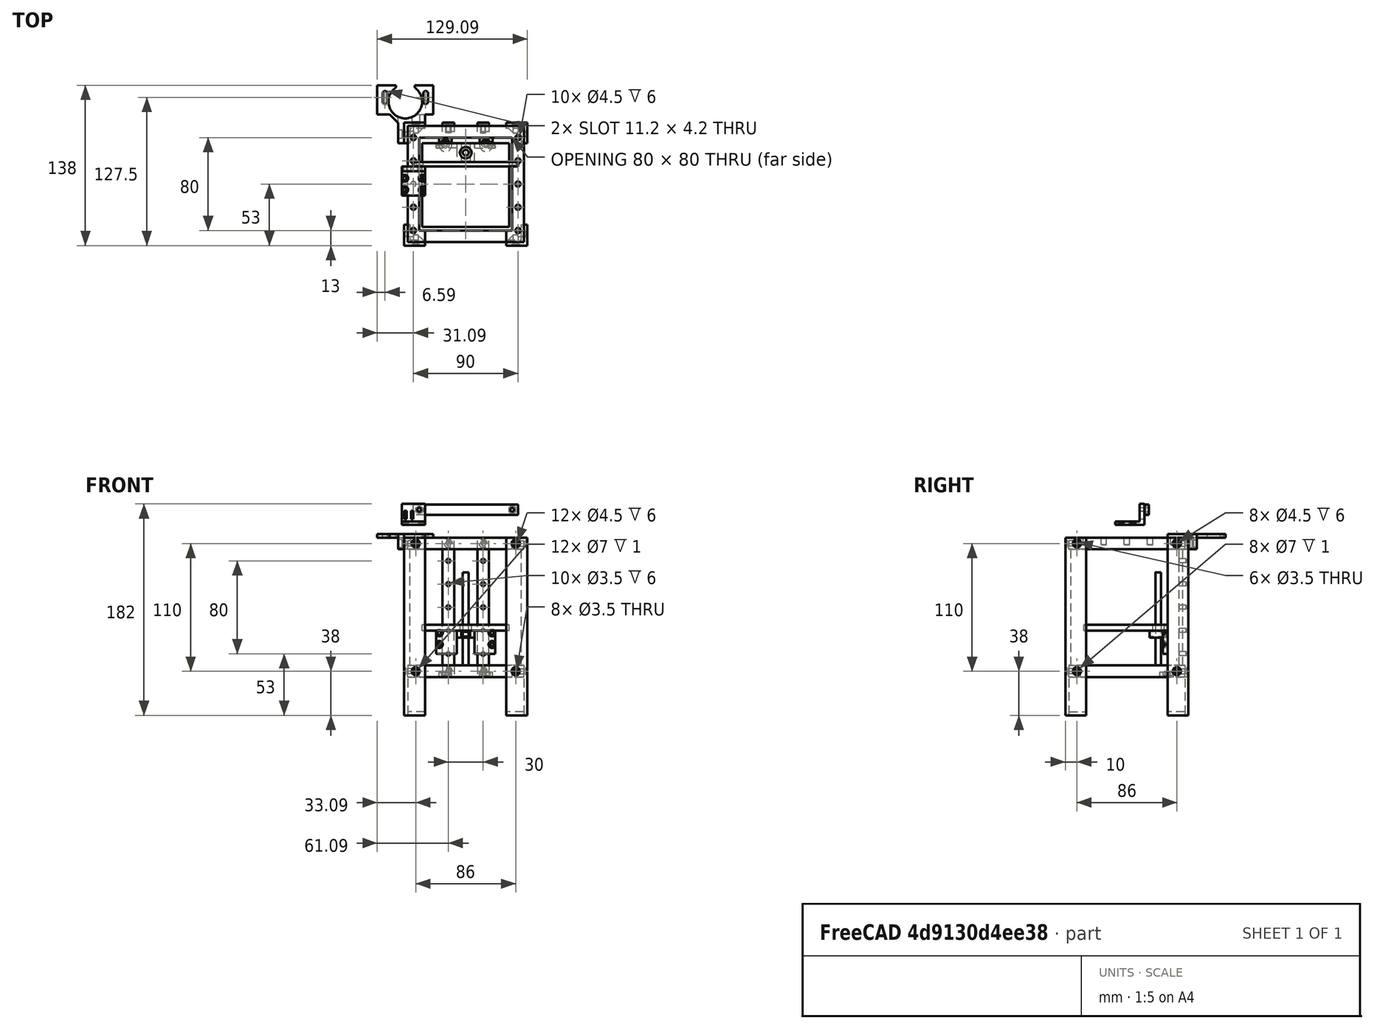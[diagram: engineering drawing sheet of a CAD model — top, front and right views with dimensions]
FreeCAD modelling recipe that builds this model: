
FCSTD DOCUMENT  (FreeCAD 0.19R24267 +99 (Git))
Label: cad
License: All rights reserved
LicenseURL: http://en.wikipedia.org/wiki/All_rights_reserved
objects: Sketcher::SketchObject×95, PartDesign::Pocket×61, PartDesign::Pad×34, Mesh::Feature×14, PartDesign::Body×13, PartDesign::Mirrored×6, PartDesign::PolarPattern×4
note: 308 computed .brp shape members not serialized (recipe doc carries the construction recipe); baked Part::Feature solids carry a one-line shape summary decoded from their .brp

FEATURE [Sketcher::SketchObject] Sketch
  FullyConstrained = true
  MapMode = 5
  Support = -> [XY_Plane]
  sketch-geometry (8):
    g0: LineSegment StartX=-50 StartY=50 StartZ=0 EndX=50 EndY=50 EndZ=0
    g1: LineSegment StartX=50 StartY=50 StartZ=0 EndX=50 EndY=-50 EndZ=0
    g2: LineSegment StartX=50 StartY=-50 StartZ=0 EndX=-50 EndY=-50 EndZ=0
    g3: LineSegment StartX=-50 StartY=-50 StartZ=0 EndX=-50 EndY=50 EndZ=0
    g4: LineSegment StartX=-40 StartY=40 StartZ=0 EndX=40 EndY=40 EndZ=0
    g5: LineSegment StartX=40 StartY=40 StartZ=0 EndX=40 EndY=-40 EndZ=0
    g6: LineSegment StartX=40 StartY=-40 StartZ=0 EndX=-40 EndY=-40 EndZ=0
    g7: LineSegment StartX=-40 StartY=-40 StartZ=0 EndX=-40 EndY=40 EndZ=0
  constraints (20):
    c: Coincident(g0,g1)
    c: Coincident(g1,g2)
    c: Coincident(g2,g3)
    c: Coincident(g3,g0)
    c: Horizontal(g2)
    c: Vertical(g1)
    c: Coincident(g4,g5)
    c: Coincident(g5,g6)
    c: Coincident(g6,g7)
    c: Coincident(g7,g4)
    c: Horizontal(g6)
    c: Vertical(g5)
    c: Symmetric(g4,g4,g-2)
    c: Symmetric(g4,g6,g-1)
    c: Equal(g7,g4)
    c: Equal(g0,g3)
    c: Symmetric(g0,g2,g-1)
    c: Symmetric(g0,g0,g-2)
    c: DistanceY(g4,g0) = 10
    c: DistanceY(g3,g3) = 100
FEATURE [PartDesign::Pad] Pad
  Direction = (1,1,1)
  Length = 10
  Length2 = 100
  Profile = -> Sketch
  Type = 0
FEATURE [Sketcher::SketchObject] Sketch002
  ExternalGeometry = -> [Pad]
  FullyConstrained = true
  MapMode = 5
  Placement = pos=(0,0,10) rot=(0,0,1;0rad)
  Support = -> [Pad]
  sketch-geometry (9):
    g0: Circle CenterX=-45 CenterY=40 CenterZ=0 NormalX=0 NormalY=0 NormalZ=1 AngleXU=0 Radius=2.25
    g1: LineSegment StartX=-45 StartY=40 StartZ=0 EndX=-50 EndY=40 EndZ=0
    g2: LineSegment StartX=-40 StartY=40 StartZ=0 EndX=-40 EndY=50 EndZ=0
    g3: LineSegment StartX=-45 StartY=40 StartZ=0 EndX=-40 EndY=40 EndZ=0
    g4: Circle CenterX=-45 CenterY=20 CenterZ=0 NormalX=0 NormalY=0 NormalZ=1 AngleXU=0 Radius=2.25
    g5: Circle CenterX=-45 CenterY=1.8e-15 CenterZ=0 NormalX=0 NormalY=0 NormalZ=1 AngleXU=0 Radius=2.25
    g6: Circle CenterX=-45 CenterY=-20 CenterZ=0 NormalX=0 NormalY=0 NormalZ=1 AngleXU=0 Radius=2.25
    g7: Circle CenterX=-45 CenterY=-40 CenterZ=0 NormalX=0 NormalY=0 NormalZ=1 AngleXU=0 Radius=2.25
    g8: LineSegment StartX=-45 StartY=40 StartZ=0 EndX=-45 EndY=-50 EndZ=0
  constraints (27):
    c: Radius(g0) = 2.25
    c: Coincident(g1,g0)
    c: PointOnObject(g1,g-3)
    c: Horizontal(g1)
    c: Coincident(g2,g-4)
    c: Vertical(g2)
    c: Coincident(g3,g0)
    c: Horizontal(g3)
    c: PointOnObject(g3,g2)
    c: Equal(g1,g3)
    c: DistanceY(g0,g-3) = 10
    c: PointOnObject(g2,g-5)
    c: Equal(g0,g4)
    c: Equal(g4,g5)
    c: Equal(g5,g6)
    c: Equal(g6,g7)
    c: Coincident(g8,g0)
    c: PointOnObject(g8,g-6)
    c: Vertical(g8)
    c: PointOnObject(g7,g8)
    c: PointOnObject(g6,g8)
    c: PointOnObject(g5,g8)
    c: PointOnObject(g4,g8)
    c: DistanceY(g4,g0) = 20
    c: DistanceY(g5,g4) = 20
    c: DistanceY(g6,g5) = 20
    c: DistanceY(g7,g6) = 20
FEATURE [PartDesign::Pocket] Pocket
  BaseFeature = -> Pad
  Length = 6
  Length2 = 100
  Profile = -> Sketch002
  Type = 0
FEATURE [PartDesign::Mirrored] Mirrored
  BaseFeature = -> Pocket
  MirrorPlane = -> Sketch002 [V_Axis]
  Originals = -> [Pocket]
FEATURE [Sketcher::SketchObject] Sketch003
  FullyConstrained = true
  MapMode = 5
  Support = -> [XY_Plane002]
  sketch-geometry (4):
    g0: LineSegment StartX=-20 StartY=53 StartZ=0 EndX=-10 EndY=53 EndZ=0
    g1: LineSegment StartX=-10 StartY=53 StartZ=0 EndX=-10 EndY=45 EndZ=0
    g2: LineSegment StartX=-10 StartY=45 StartZ=0 EndX=-20 EndY=45 EndZ=0
    g3: LineSegment StartX=-20 StartY=45 StartZ=0 EndX=-20 EndY=53 EndZ=0
  constraints (12):
    c: Coincident(g0,g1)
    c: Coincident(g1,g2)
    c: Coincident(g2,g3)
    c: Coincident(g3,g0)
    c: Horizontal(g0)
    c: Horizontal(g2)
    c: Vertical(g1)
    c: Vertical(g3)
    c: DistanceY(g3,g3) = 8
    c: DistanceY(g-1,g1) = 45
    c: DistanceX(g0,g0) = 10
    c: DistanceX(g0,g-1) = 10
FEATURE [PartDesign::Pad] Pad002
  Direction = (1,1,1)
  Length = 100
  Length2 = 100
  Profile = -> Sketch003
  Type = 0
FEATURE [Sketcher::SketchObject] Sketch004
  ExternalGeometry = -> [Pad002]
  FullyConstrained = true
  MapMode = 5
  Placement = pos=(0,0,100) rot=(0,0,1;0rad)
  Support = -> [Pad002]
  sketch-geometry (4):
    g0: LineSegment StartX=-10 StartY=53 StartZ=0 EndX=-20 EndY=53 EndZ=0
    g1: LineSegment StartX=-20 StartY=53 StartZ=0 EndX=-20 EndY=50 EndZ=0
    g2: LineSegment StartX=-20 StartY=50 StartZ=0 EndX=-10 EndY=50 EndZ=0
    g3: LineSegment StartX=-10 StartY=50 StartZ=0 EndX=-10 EndY=53 EndZ=0
  constraints (11):
    c: Coincident(g0,g1)
    c: Coincident(g1,g2)
    c: Coincident(g2,g3)
    c: Coincident(g3,g0)
    c: Horizontal(g0)
    c: Horizontal(g2)
    c: Vertical(g1)
    c: Vertical(g3)
    c: Coincident(g0,g-3)
    c: PointOnObject(g1,g-4)
    c: DistanceY(g3,g3) = 3
FEATURE [PartDesign::Pad] Pad003
  BaseFeature = -> Pad002
  Direction = (1,1,1)
  Length = 10
  Length2 = 100
  Profile = -> Sketch004
  Type = 0
FEATURE [Sketcher::SketchObject] Sketch005
  ExternalGeometry = -> [Pad003]
  FullyConstrained = true
  MapMode = 5
  Placement = pos=(0,53,0) rot=(0,0.707107,0.707107;3.14159rad)
  Support = -> [Pad003]
  sketch-geometry (4):
    g0: Circle CenterX=15 CenterY=105 CenterZ=0 NormalX=0 NormalY=0 NormalZ=1 AngleXU=0 Radius=1.7
    g1: LineSegment StartX=15 StartY=105 StartZ=0 EndX=10 EndY=110 EndZ=0
    g2: LineSegment StartX=15 StartY=105 StartZ=0 EndX=10 EndY=100 EndZ=0
    g3: LineSegment StartX=15 StartY=105 StartZ=0 EndX=20 EndY=110 EndZ=0
  constraints (9):
    c: Radius(g0) = 1.7
    c: Coincident(g1,g-3)
    c: Coincident(g2,g-3)
    c: Coincident(g3,g-4)
    c: Equal(g1,g3)
    c: Equal(g3,g2)
    c: Coincident(g0,g1)
    c: Coincident(g0,g3)
    c: Coincident(g0,g2)
FEATURE [PartDesign::Pocket] Pocket001
  BaseFeature = -> Pad003
  Length = 5
  Length2 = 100
  Profile = -> Sketch005
  Type = 0
FEATURE [Sketcher::SketchObject] Sketch006
  ExternalGeometry = -> [Pocket001]
  FullyConstrained = true
  MapMode = 5
  Placement = pos=(0,53,0) rot=(0,0.707107,0.707107;3.14159rad)
  Support = -> [Pocket001]
  sketch-geometry (1):
    g0: Circle CenterX=15 CenterY=105 CenterZ=0 NormalX=0 NormalY=0 NormalZ=1 AngleXU=0 Radius=3.5
  constraints (2):
    c: Coincident(g0,g-3)
    c: Radius(g0) = 3.5
FEATURE [PartDesign::Pocket] Pocket002
  BaseFeature = -> Pocket001
  Length = 1
  Length2 = 100
  Profile = -> Sketch006
  Type = 0
FEATURE [Sketcher::SketchObject] Sketch007
  ExternalGeometry = -> [Pocket002]
  FullyConstrained = true
  MapMode = 5
  Placement = pos=(0,0,0) rot=(1,0,0;3.14159rad)
  Support = -> [Pocket002]
  sketch-geometry (4):
    g0: LineSegment StartX=-10 StartY=-53 StartZ=0 EndX=-20 EndY=-53 EndZ=0
    g1: LineSegment StartX=-20 StartY=-53 StartZ=0 EndX=-20 EndY=-50 EndZ=0
    g2: LineSegment StartX=-20 StartY=-50 StartZ=0 EndX=-10 EndY=-50 EndZ=0
    g3: LineSegment StartX=-10 StartY=-50 StartZ=0 EndX=-10 EndY=-53 EndZ=0
  constraints (11):
    c: Coincident(g0,g1)
    c: Coincident(g1,g2)
    c: Coincident(g2,g3)
    c: Coincident(g3,g0)
    c: Horizontal(g0)
    c: Horizontal(g2)
    c: Vertical(g1)
    c: Vertical(g3)
    c: Coincident(g0,g-4)
    c: PointOnObject(g1,g-3)
    c: DistanceY(g3,g3) = 3
FEATURE [PartDesign::Pad] Pad004
  BaseFeature = -> Pocket002
  Direction = (1,1,1)
  Length = 10
  Length2 = 100
  Profile = -> Sketch007
  Type = 0
FEATURE [Sketcher::SketchObject] Sketch008
  ExternalGeometry = -> [Pad004]
  FullyConstrained = true
  MapMode = 5
  Placement = pos=(0,53,0) rot=(0,0.707107,0.707107;3.14159rad)
  Support = -> [Pad004]
  sketch-geometry (4):
    g0: Circle CenterX=15 CenterY=-5 CenterZ=0 NormalX=0 NormalY=0 NormalZ=1 AngleXU=0 Radius=1.75
    g1: LineSegment StartX=15 StartY=-5 StartZ=0 EndX=10 EndY=0 EndZ=0
    g2: LineSegment StartX=15 StartY=-5 StartZ=0 EndX=10 EndY=-10 EndZ=0
    g3: LineSegment StartX=15 StartY=-5 StartZ=0 EndX=20 EndY=-10 EndZ=0
  constraints (9):
    c: Coincident(g1,g0)
    c: Coincident(g1,g-3)
    c: Coincident(g2,g0)
    c: Coincident(g2,g-4)
    c: Coincident(g3,g0)
    c: Coincident(g3,g-4)
    c: Equal(g3,g2)
    c: Equal(g2,g1)
    c: Radius(g0) = 1.75
FEATURE [PartDesign::Pocket] Pocket003
  BaseFeature = -> Pad004
  Length = 5
  Length2 = 100
  Profile = -> Sketch008
  Type = 0
FEATURE [Sketcher::SketchObject] Sketch009
  ExternalGeometry = -> [Pocket003]
  FullyConstrained = true
  MapMode = 5
  Placement = pos=(0,53,0) rot=(0,0.707107,0.707107;3.14159rad)
  Support = -> [Pocket003]
  sketch-geometry (1):
    g0: Circle CenterX=15 CenterY=-5 CenterZ=0 NormalX=0 NormalY=0 NormalZ=1 AngleXU=0 Radius=3.5
  constraints (2):
    c: Coincident(g0,g-3)
    c: Radius(g0) = 3.5
FEATURE [PartDesign::Pocket] Pocket004
  BaseFeature = -> Pocket003
  Length = 1
  Length2 = 100
  Profile = -> Sketch009
  Type = 0
FEATURE [Sketcher::SketchObject] Sketch010
  ExternalGeometry = -> [Pocket004]
  FullyConstrained = true
  MapMode = 5
  Placement = pos=(0,45,0) rot=(1,0,0;1.5708rad)
  Support = -> [Pocket004]
  sketch-geometry (6):
    g0: Circle CenterX=-15 CenterY=90 CenterZ=0 NormalX=0 NormalY=0 NormalZ=1 AngleXU=0 Radius=1.75
    g1: Circle CenterX=-15 CenterY=70 CenterZ=0 NormalX=0 NormalY=0 NormalZ=1 AngleXU=0 Radius=1.75
    g2: Circle CenterX=-15 CenterY=50 CenterZ=0 NormalX=0 NormalY=0 NormalZ=1 AngleXU=0 Radius=1.75
    g3: Circle CenterX=-15 CenterY=30 CenterZ=0 NormalX=0 NormalY=0 NormalZ=1 AngleXU=0 Radius=1.75
    g4: Circle CenterX=-15 CenterY=10 CenterZ=0 NormalX=0 NormalY=0 NormalZ=1 AngleXU=0 Radius=1.75
    g5: LineSegment StartX=-15 StartY=100 StartZ=0 EndX=-15 EndY=0 EndZ=0
  constraints (19):
    c: Equal(g0,g1)
    c: Equal(g1,g2)
    c: Equal(g2,g3)
    c: Equal(g3,g4)
    c: Radius(g0) = 1.75
    c: PointOnObject(g5,g-5)
    c: PointOnObject(g5,g-1)
    c: Vertical(g5)
    c: DistanceX(g-5,g5) = 5
    c: PointOnObject(g0,g5)
    c: PointOnObject(g1,g5)
    c: PointOnObject(g2,g5)
    c: PointOnObject(g3,g5)
    c: PointOnObject(g4,g5)
    c: DistanceY(g1,g0) = 20
    c: DistanceY(g2,g1) = 20
    c: DistanceY(g3,g2) = 20
    c: DistanceY(g4,g3) = 20
    c: DistanceY(g0,g5) = 10
FEATURE [PartDesign::Pocket] Pocket005
  BaseFeature = -> Pocket004
  Length = 6
  Length2 = 100
  Profile = -> Sketch010
  Type = 0
FEATURE [PartDesign::Body] Body002  label="z_rail"
  Group = -> [Sketch003,Pad002,Sketch004,Pad003,Sketch005,Pocket001,Sketch006,Pocket002,Sketch007,Pad004,Sketch008,Pocket003,Sketch009,Pocket004,Sketch010,Pocket005]
  Origin = -> Origin002
  Tip = -> Pocket005
FEATURE [Sketcher::SketchObject] Sketch016
  FullyConstrained = true
  MapMode = 5
  Support = -> [XY_Plane003]
  sketch-geometry (4):
    g0: LineSegment StartX=-20 StartY=53 StartZ=0 EndX=-10 EndY=53 EndZ=0
    g1: LineSegment StartX=-10 StartY=53 StartZ=0 EndX=-10 EndY=45 EndZ=0
    g2: LineSegment StartX=-10 StartY=45 StartZ=0 EndX=-20 EndY=45 EndZ=0
    g3: LineSegment StartX=-20 StartY=45 StartZ=0 EndX=-20 EndY=53 EndZ=0
  constraints (12):
    c: Coincident(g0,g1)
    c: Coincident(g1,g2)
    c: Coincident(g2,g3)
    c: Coincident(g3,g0)
    c: Horizontal(g0)
    c: Horizontal(g2)
    c: Vertical(g1)
    c: Vertical(g3)
    c: DistanceY(g3,g3) = 8
    c: DistanceY(g-1,g1) = 45
    c: DistanceX(g0,g0) = 10
    c: DistanceX(g0,g-1) = 10
FEATURE [PartDesign::Pad] Pad005
  Direction = (1,1,1)
  Length = 100
  Length2 = 100
  Profile = -> Sketch016
  Type = 0
FEATURE [Sketcher::SketchObject] Sketch015
  ExternalGeometry = -> [Pad005]
  FullyConstrained = true
  MapMode = 5
  Placement = pos=(0,0,100) rot=(0,0,1;0rad)
  Support = -> [Pad005]
  sketch-geometry (4):
    g0: LineSegment StartX=-10 StartY=53 StartZ=0 EndX=-20 EndY=53 EndZ=0
    g1: LineSegment StartX=-20 StartY=53 StartZ=0 EndX=-20 EndY=50 EndZ=0
    g2: LineSegment StartX=-20 StartY=50 StartZ=0 EndX=-10 EndY=50 EndZ=0
    g3: LineSegment StartX=-10 StartY=50 StartZ=0 EndX=-10 EndY=53 EndZ=0
  constraints (11):
    c: Coincident(g0,g1)
    c: Coincident(g1,g2)
    c: Coincident(g2,g3)
    c: Coincident(g3,g0)
    c: Horizontal(g0)
    c: Horizontal(g2)
    c: Vertical(g1)
    c: Vertical(g3)
    c: Coincident(g0,g-3)
    c: PointOnObject(g1,g-4)
    c: DistanceY(g3,g3) = 3
FEATURE [PartDesign::Pad] Pad006
  BaseFeature = -> Pad005
  Direction = (1,1,1)
  Length = 10
  Length2 = 100
  Profile = -> Sketch015
  Type = 0
FEATURE [Sketcher::SketchObject] Sketch017
  ExternalGeometry = -> [Pad006]
  FullyConstrained = true
  MapMode = 5
  Placement = pos=(0,53,0) rot=(0,0.707107,0.707107;3.14159rad)
  Support = -> [Pad006]
  sketch-geometry (4):
    g0: Circle CenterX=15 CenterY=105 CenterZ=0 NormalX=0 NormalY=0 NormalZ=1 AngleXU=0 Radius=1.7
    g1: LineSegment StartX=15 StartY=105 StartZ=0 EndX=10 EndY=110 EndZ=0
    g2: LineSegment StartX=15 StartY=105 StartZ=0 EndX=10 EndY=100 EndZ=0
    g3: LineSegment StartX=15 StartY=105 StartZ=0 EndX=20 EndY=110 EndZ=0
  constraints (9):
    c: Radius(g0) = 1.7
    c: Coincident(g1,g-3)
    c: Coincident(g2,g-3)
    c: Coincident(g3,g-4)
    c: Equal(g1,g3)
    c: Equal(g3,g2)
    c: Coincident(g0,g1)
    c: Coincident(g0,g3)
    c: Coincident(g0,g2)
FEATURE [PartDesign::Pocket] Pocket006
  BaseFeature = -> Pad006
  Length = 5
  Length2 = 100
  Profile = -> Sketch017
  Type = 0
FEATURE [Sketcher::SketchObject] Sketch013
  ExternalGeometry = -> [Pocket006]
  FullyConstrained = true
  MapMode = 5
  Placement = pos=(0,53,0) rot=(0,0.707107,0.707107;3.14159rad)
  Support = -> [Pocket006]
  sketch-geometry (1):
    g0: Circle CenterX=15 CenterY=105 CenterZ=0 NormalX=0 NormalY=0 NormalZ=1 AngleXU=0 Radius=3.5
  constraints (2):
    c: Coincident(g0,g-3)
    c: Radius(g0) = 3.5
FEATURE [PartDesign::Pocket] Pocket008
  BaseFeature = -> Pocket006
  Length = 1
  Length2 = 100
  Profile = -> Sketch013
  Type = 0
FEATURE [Sketcher::SketchObject] Sketch012
  ExternalGeometry = -> [Pocket008]
  FullyConstrained = true
  MapMode = 5
  Placement = pos=(0,0,0) rot=(1,0,0;3.14159rad)
  Support = -> [Pocket008]
  sketch-geometry (4):
    g0: LineSegment StartX=-10 StartY=-53 StartZ=0 EndX=-20 EndY=-53 EndZ=0
    g1: LineSegment StartX=-20 StartY=-53 StartZ=0 EndX=-20 EndY=-50 EndZ=0
    g2: LineSegment StartX=-20 StartY=-50 StartZ=0 EndX=-10 EndY=-50 EndZ=0
    g3: LineSegment StartX=-10 StartY=-50 StartZ=0 EndX=-10 EndY=-53 EndZ=0
  constraints (11):
    c: Coincident(g0,g1)
    c: Coincident(g1,g2)
    c: Coincident(g2,g3)
    c: Coincident(g3,g0)
    c: Horizontal(g0)
    c: Horizontal(g2)
    c: Vertical(g1)
    c: Vertical(g3)
    c: Coincident(g0,g-4)
    c: PointOnObject(g1,g-3)
    c: DistanceY(g3,g3) = 3
FEATURE [PartDesign::Pad] Pad007
  BaseFeature = -> Pocket008
  Direction = (1,1,1)
  Length = 10
  Length2 = 100
  Profile = -> Sketch012
  Type = 0
FEATURE [Sketcher::SketchObject] Sketch011
  ExternalGeometry = -> [Pad007]
  FullyConstrained = true
  MapMode = 5
  Placement = pos=(0,53,0) rot=(0,0.707107,0.707107;3.14159rad)
  Support = -> [Pad007]
  sketch-geometry (4):
    g0: Circle CenterX=15 CenterY=-5 CenterZ=0 NormalX=0 NormalY=0 NormalZ=1 AngleXU=0 Radius=1.75
    g1: LineSegment StartX=15 StartY=-5 StartZ=0 EndX=10 EndY=0 EndZ=0
    g2: LineSegment StartX=15 StartY=-5 StartZ=0 EndX=10 EndY=-10 EndZ=0
    g3: LineSegment StartX=15 StartY=-5 StartZ=0 EndX=20 EndY=-10 EndZ=0
  constraints (9):
    c: Coincident(g1,g0)
    c: Coincident(g1,g-3)
    c: Coincident(g2,g0)
    c: Coincident(g2,g-4)
    c: Coincident(g3,g0)
    c: Coincident(g3,g-4)
    c: Equal(g3,g2)
    c: Equal(g2,g1)
    c: Radius(g0) = 1.75
FEATURE [PartDesign::Pocket] Pocket007
  BaseFeature = -> Pad007
  Length = 5
  Length2 = 100
  Profile = -> Sketch011
  Type = 0
FEATURE [Sketcher::SketchObject] Sketch014
  ExternalGeometry = -> [Pocket007]
  FullyConstrained = true
  MapMode = 5
  Placement = pos=(0,53,0) rot=(0,0.707107,0.707107;3.14159rad)
  Support = -> [Pocket007]
  sketch-geometry (1):
    g0: Circle CenterX=15 CenterY=-5 CenterZ=0 NormalX=0 NormalY=0 NormalZ=1 AngleXU=0 Radius=3.5
  constraints (2):
    c: Coincident(g0,g-3)
    c: Radius(g0) = 3.5
FEATURE [PartDesign::Pocket] Pocket010
  BaseFeature = -> Pocket007
  Length = 1
  Length2 = 100
  Profile = -> Sketch014
  Type = 0
FEATURE [Sketcher::SketchObject] Sketch018
  ExternalGeometry = -> [Pocket010]
  FullyConstrained = true
  MapMode = 5
  Placement = pos=(0,45,0) rot=(1,0,0;1.5708rad)
  Support = -> [Pocket010]
  sketch-geometry (6):
    g0: Circle CenterX=-15 CenterY=90 CenterZ=0 NormalX=0 NormalY=0 NormalZ=1 AngleXU=0 Radius=1.75
    g1: Circle CenterX=-15 CenterY=70 CenterZ=0 NormalX=0 NormalY=0 NormalZ=1 AngleXU=0 Radius=1.75
    g2: Circle CenterX=-15 CenterY=50 CenterZ=0 NormalX=0 NormalY=0 NormalZ=1 AngleXU=0 Radius=1.75
    g3: Circle CenterX=-15 CenterY=30 CenterZ=0 NormalX=0 NormalY=0 NormalZ=1 AngleXU=0 Radius=1.75
    g4: Circle CenterX=-15 CenterY=10 CenterZ=0 NormalX=0 NormalY=0 NormalZ=1 AngleXU=0 Radius=1.75
    g5: LineSegment StartX=-15 StartY=100 StartZ=0 EndX=-15 EndY=0 EndZ=0
  constraints (19):
    c: Equal(g0,g1)
    c: Equal(g1,g2)
    c: Equal(g2,g3)
    c: Equal(g3,g4)
    c: Radius(g0) = 1.75
    c: PointOnObject(g5,g-5)
    c: PointOnObject(g5,g-1)
    c: Vertical(g5)
    c: DistanceX(g-5,g5) = 5
    c: PointOnObject(g0,g5)
    c: PointOnObject(g1,g5)
    c: PointOnObject(g2,g5)
    c: PointOnObject(g3,g5)
    c: PointOnObject(g4,g5)
    c: DistanceY(g1,g0) = 20
    c: DistanceY(g2,g1) = 20
    c: DistanceY(g3,g2) = 20
    c: DistanceY(g4,g3) = 20
    c: DistanceY(g0,g5) = 10
FEATURE [PartDesign::Pocket] Pocket009
  BaseFeature = -> Pocket010
  Length = 6
  Length2 = 100
  Profile = -> Sketch018
  Type = 0
FEATURE [PartDesign::Body] Body003  label="z_rail001"
  Group = -> [Sketch016,Pad005,Sketch015,Pad006,Sketch017,Pocket006,Sketch013,Pocket008,Sketch012,Pad007,Sketch011,Pocket007,Sketch014,Pocket010,Sketch018,Pocket009]
  Origin = -> Origin003
  Placement = pos=(30,0,0) rot=(0,0,1;0rad)
  Tip = -> Pocket009
FEATURE [Sketcher::SketchObject] Sketch019
  FullyConstrained = true
  MapMode = 5
  Support = -> [XY_Plane004]
  sketch-geometry (6):
    g0: LineSegment StartX=-53 StartY=-35 StartZ=0 EndX=-53 EndY=-53 EndZ=0
    g1: LineSegment StartX=-53 StartY=-53 StartZ=0 EndX=-35 EndY=-53 EndZ=0
    g2: LineSegment StartX=-48 StartY=-35 StartZ=0 EndX=-48 EndY=-48 EndZ=0
    g3: LineSegment StartX=-48 StartY=-48 StartZ=0 EndX=-35 EndY=-48 EndZ=0
    g4: LineSegment StartX=-48 StartY=-35 StartZ=0 EndX=-53 EndY=-35 EndZ=0
    g5: LineSegment StartX=-35 StartY=-48 StartZ=0 EndX=-35 EndY=-53 EndZ=0
  constraints (19):
    c: Vertical(g0)
    c: Coincident(g1,g0)
    c: Horizontal(g1)
    c: DistanceY(g0,g-1) = 53
    c: DistanceX(g0,g-1) = 53
    c: Vertical(g2)
    c: Coincident(g3,g2)
    c: Horizontal(g3)
    c: DistanceY(g0,g2) = 5
    c: DistanceX(g0,g2) = 5
    c: Coincident(g4,g2)
    c: Horizontal(g4)
    c: Vertical(g5)
    c: Coincident(g0,g4)
    c: Coincident(g1,g5)
    c: Equal(g0,g1)
    c: Equal(g2,g3)
    c: Equal(g4,g5)
    c: DistanceY(g0,g0) = 18
FEATURE [PartDesign::Pad] Pad008
  Direction = (1,1,1)
  Length = 100
  Length2 = 100
  Profile = -> Sketch019
  Type = 0
FEATURE [Sketcher::SketchObject] Sketch020
  ExternalGeometry = -> [Pad008]
  FullyConstrained = true
  MapMode = 5
  Placement = pos=(0,0,100) rot=(0,0,1;0rad)
  Support = -> [Pad008]
  sketch-geometry (6):
    g0: LineSegment StartX=-53 StartY=-35 StartZ=0 EndX=-53 EndY=-53 EndZ=0
    g1: LineSegment StartX=-53 StartY=-53 StartZ=0 EndX=-35 EndY=-53 EndZ=0
    g2: LineSegment StartX=-35 StartY=-53 StartZ=0 EndX=-35 EndY=-50 EndZ=0
    g3: LineSegment StartX=-35 StartY=-50 StartZ=0 EndX=-50 EndY=-50 EndZ=0
    g4: LineSegment StartX=-50 StartY=-50 StartZ=0 EndX=-50 EndY=-35 EndZ=0
    g5: LineSegment StartX=-50 StartY=-35 StartZ=0 EndX=-53 EndY=-35 EndZ=0
  constraints (15):
    c: Coincident(g-5,g0)
    c: Coincident(g0,g-4)
    c: Coincident(g0,g1)
    c: Coincident(g1,g-6)
    c: Coincident(g1,g2)
    c: PointOnObject(g2,g-6)
    c: Coincident(g2,g3)
    c: Horizontal(g3)
    c: Coincident(g3,g4)
    c: PointOnObject(g4,g-5)
    c: Vertical(g4)
    c: Coincident(g4,g5)
    c: Coincident(g5,g0)
    c: Equal(g5,g2)
    c: DistanceX(g5,g5) = 3
FEATURE [PartDesign::Pad] Pad009
  BaseFeature = -> Pad008
  Direction = (1,1,1)
  Length = 10
  Length2 = 100
  Profile = -> Sketch020
  Type = 0
FEATURE [Sketcher::SketchObject] Sketch021
  ExternalGeometry = -> [Pad009]
  FullyConstrained = true
  MapMode = 5
  Placement = pos=(0,-53,0) rot=(1,0,0;1.5708rad)
  Support = -> [Pad009]
  sketch-geometry (1):
    g0: Circle CenterX=-43 CenterY=105 CenterZ=0 NormalX=0 NormalY=0 NormalZ=1 AngleXU=0 Radius=1.6
  constraints (3):
    c: Radius(g0) = 1.6
    c: DistanceX(g-3,g0) = 10
    c: DistanceY(g0,g-3) = 5
FEATURE [PartDesign::Pocket] Pocket011
  BaseFeature = -> Pad009
  Length = 5
  Length2 = 100
  Profile = -> Sketch021
  Type = 0
FEATURE [Sketcher::SketchObject] Sketch022
  ExternalGeometry = -> [Pocket011]
  FullyConstrained = true
  MapMode = 5
  Placement = pos=(0,-53,0) rot=(1,0,0;1.5708rad)
  Support = -> [Pocket011]
  sketch-geometry (1):
    g0: Circle CenterX=-43 CenterY=105 CenterZ=0 NormalX=0 NormalY=0 NormalZ=1 AngleXU=0 Radius=3.5
  constraints (2):
    c: Coincident(g0,g-3)
    c: Radius(g0) = 3.5
FEATURE [PartDesign::Pocket] Pocket012
  BaseFeature = -> Pocket011
  Length = 1
  Length2 = 100
  Profile = -> Sketch022
  Type = 0
FEATURE [Sketcher::SketchObject] Sketch023
  ExternalGeometry = -> [Pocket012]
  FullyConstrained = true
  MapMode = 5
  Placement = pos=(-53,0,0) rot=(0.57735,-0.57735,-0.57735;2.0944rad)
  Support = -> [Pocket012]
  sketch-geometry (1):
    g0: Circle CenterX=43 CenterY=105 CenterZ=0 NormalX=0 NormalY=0 NormalZ=1 AngleXU=0 Radius=1.75
  constraints (3):
    c: Radius(g0) = 1.75
    c: DistanceX(g0,g-3) = 10
    c: DistanceY(g0,g-3) = 5
FEATURE [PartDesign::Pocket] Pocket013
  BaseFeature = -> Pocket012
  Length = 5
  Length2 = 100
  Profile = -> Sketch023
  Type = 0
FEATURE [Sketcher::SketchObject] Sketch024
  ExternalGeometry = -> [Pocket013]
  FullyConstrained = true
  MapMode = 5
  Placement = pos=(-53,0,0) rot=(0.57735,-0.57735,-0.57735;2.0944rad)
  Support = -> [Pocket013]
  sketch-geometry (1):
    g0: Circle CenterX=43 CenterY=105 CenterZ=0 NormalX=0 NormalY=0 NormalZ=1 AngleXU=0 Radius=3.5
  constraints (2):
    c: Coincident(g0,g-3)
    c: Radius(g0) = 3.5
FEATURE [PartDesign::Pocket] Pocket014
  BaseFeature = -> Pocket013
  Length = 1
  Length2 = 100
  Profile = -> Sketch024
  Type = 0
FEATURE [Sketcher::SketchObject] Sketch025
  ExternalGeometry = -> [Pocket014]
  FullyConstrained = true
  MapMode = 5
  Placement = pos=(0,0,0) rot=(1,0,0;3.14159rad)
  Support = -> [Pocket014]
  sketch-geometry (6):
    g0: LineSegment StartX=-35 StartY=53 StartZ=0 EndX=-53 EndY=53 EndZ=0
    g1: LineSegment StartX=-53 StartY=53 StartZ=0 EndX=-53 EndY=35 EndZ=0
    g2: LineSegment StartX=-53 StartY=35 StartZ=0 EndX=-50 EndY=35 EndZ=0
    g3: LineSegment StartX=-50 StartY=35 StartZ=0 EndX=-50 EndY=50 EndZ=0
    g4: LineSegment StartX=-50 StartY=50 StartZ=0 EndX=-35 EndY=50 EndZ=0
    g5: LineSegment StartX=-35 StartY=50 StartZ=0 EndX=-35 EndY=53 EndZ=0
  constraints (15):
    c: Coincident(g-6,g0)
    c: Coincident(g0,g-4)
    c: Coincident(g0,g1)
    c: Coincident(g1,g-5)
    c: Coincident(g1,g2)
    c: PointOnObject(g2,g-5)
    c: Coincident(g2,g3)
    c: Vertical(g3)
    c: Coincident(g3,g4)
    c: PointOnObject(g4,g-6)
    c: Horizontal(g4)
    c: Coincident(g4,g5)
    c: Coincident(g5,g0)
    c: Equal(g5,g2)
    c: DistanceY(g5,g5) = 3
FEATURE [PartDesign::Pad] Pad010
  BaseFeature = -> Pocket014
  Direction = (1,1,1)
  Length = 40
  Length2 = 100
  Profile = -> Sketch025
  Type = 0
FEATURE [Sketcher::SketchObject] Sketch026
  ExternalGeometry = -> [Pad010]
  FullyConstrained = true
  MapMode = 5
  Placement = pos=(0,0,-40) rot=(1,0,0;3.14159rad)
  Support = -> [Pad010]
  sketch-geometry (5):
    g0: LineSegment StartX=-35 StartY=50 StartZ=0 EndX=-35 EndY=53 EndZ=0
    g1: LineSegment StartX=-35 StartY=53 StartZ=0 EndX=-53 EndY=53 EndZ=0
    g2: LineSegment StartX=-53 StartY=53 StartZ=0 EndX=-53 EndY=35 EndZ=0
    g3: LineSegment StartX=-53 StartY=35 StartZ=0 EndX=-50 EndY=35 EndZ=0
    g4: LineSegment StartX=-50 StartY=35 StartZ=0 EndX=-35 EndY=50 EndZ=0
  constraints (10):
    c: Coincident(g-5,g0)
    c: Coincident(g0,g-5)
    c: Coincident(g0,g1)
    c: Coincident(g1,g-4)
    c: Coincident(g1,g2)
    c: Coincident(g2,g-6)
    c: Coincident(g2,g3)
    c: Coincident(g3,g-6)
    c: Coincident(g3,g4)
    c: Coincident(g4,g0)
FEATURE [PartDesign::Pad] Pad011
  BaseFeature = -> Pad010
  Direction = (1,1,1)
  Length = 3
  Length2 = 100
  Profile = -> Sketch026
  Type = 0
FEATURE [Sketcher::SketchObject] Sketch027
  ExternalGeometry = -> [Pad011]
  FullyConstrained = true
  MapMode = 5
  Placement = pos=(-53,0,0) rot=(0.57735,-0.57735,-0.57735;2.0944rad)
  Support = -> [Pad011]
  sketch-geometry (1):
    g0: Circle CenterX=43 CenterY=-5 CenterZ=0 NormalX=0 NormalY=0 NormalZ=1 AngleXU=0 Radius=1.75
  constraints (3):
    c: Radius(g0) = 1.75
    c: DistanceY(g0,g-4) = 5
    c: DistanceX(g0,g-4) = 10
FEATURE [PartDesign::Pocket] Pocket015
  BaseFeature = -> Pad011
  Length = 5
  Length2 = 100
  Profile = -> Sketch027
  Type = 0
FEATURE [Sketcher::SketchObject] Sketch028
  ExternalGeometry = -> [Pocket015]
  FullyConstrained = true
  MapMode = 5
  Placement = pos=(-53,0,0) rot=(0.57735,-0.57735,-0.57735;2.0944rad)
  Support = -> [Pocket015]
  sketch-geometry (1):
    g0: Circle CenterX=43 CenterY=-5 CenterZ=0 NormalX=0 NormalY=0 NormalZ=1 AngleXU=0 Radius=3.5
  constraints (2):
    c: Coincident(g0,g-3)
    c: Radius(g0) = 3.5
FEATURE [PartDesign::Pocket] Pocket016
  BaseFeature = -> Pocket015
  Length = 1
  Length2 = 100
  Profile = -> Sketch028
  Type = 0
FEATURE [Sketcher::SketchObject] Sketch029
  ExternalGeometry = -> [Pocket016]
  FullyConstrained = true
  MapMode = 5
  Placement = pos=(0,-53,0) rot=(1,0,0;1.5708rad)
  Support = -> [Pocket016]
  sketch-geometry (1):
    g0: Circle CenterX=-43 CenterY=-5 CenterZ=0 NormalX=0 NormalY=0 NormalZ=1 AngleXU=0 Radius=1.75
  constraints (3):
    c: DistanceX(g-3,g0) = 10
    c: DistanceY(g0,g-4) = 5
    c: Radius(g0) = 1.75
FEATURE [PartDesign::Pocket] Pocket017
  BaseFeature = -> Pocket016
  Length = 5
  Length2 = 100
  Profile = -> Sketch029
  Type = 0
FEATURE [Sketcher::SketchObject] Sketch030
  ExternalGeometry = -> [Pocket017]
  FullyConstrained = true
  MapMode = 5
  Placement = pos=(0,-53,0) rot=(1,0,0;1.5708rad)
  Support = -> [Pocket017]
  sketch-geometry (1):
    g0: Circle CenterX=-43 CenterY=-5 CenterZ=0 NormalX=0 NormalY=0 NormalZ=1 AngleXU=0 Radius=3.5
  constraints (2):
    c: Coincident(g0,g-3)
    c: Radius(g0) = 3.5
FEATURE [PartDesign::Pocket] Pocket018
  BaseFeature = -> Pocket017
  Length = 1
  Length2 = 100
  Profile = -> Sketch030
  Type = 0
FEATURE [PartDesign::Body] Body004  label="side_frame"
  Group = -> [Sketch019,Pad008,Sketch020,Pad009,Sketch021,Pocket011,Sketch022,Pocket012,Sketch023,Pocket013,Sketch024,Pocket014,Sketch025,Pad010,Sketch026,Pad011,Sketch027,Pocket015,Sketch028,Pocket016,Sketch029,Pocket017,Sketch030,Pocket018]
  Origin = -> Origin004
  Tip = -> Pocket018
FEATURE [Mesh::Feature] _00mm_rail  label="z_rail_0"
  Placement = pos=(-105,232,2) rot=(0,0,1;4.71239rad)
FEATURE [Mesh::Feature] _00mm_rail001  label="z_rail_1"
  Placement = pos=(-135,232,2) rot=(0,0,1;4.71239rad)
FEATURE [Mesh::Feature] _00mm_rail_flat  label="y_rail_0"
  Placement = pos=(75,-191,107) rot=(0,0,1;1.5708rad)
FEATURE [Mesh::Feature] _00mm_rail_flat001  label="y_rail_1"
  Placement = pos=(165,-191,107) rot=(0,0,1;1.5708rad)
FEATURE [Sketcher::SketchObject] Sketch032
  FullyConstrained = true
  MapMode = 5
  Support = -> [XY_Plane005]
  sketch-geometry (6):
    g0: LineSegment StartX=-53 StartY=-35 StartZ=0 EndX=-53 EndY=-53 EndZ=0
    g1: LineSegment StartX=-53 StartY=-53 StartZ=0 EndX=-35 EndY=-53 EndZ=0
    g2: LineSegment StartX=-48 StartY=-35 StartZ=0 EndX=-48 EndY=-48 EndZ=0
    g3: LineSegment StartX=-48 StartY=-48 StartZ=0 EndX=-35 EndY=-48 EndZ=0
    g4: LineSegment StartX=-48 StartY=-35 StartZ=0 EndX=-53 EndY=-35 EndZ=0
    g5: LineSegment StartX=-35 StartY=-48 StartZ=0 EndX=-35 EndY=-53 EndZ=0
  constraints (19):
    c: Vertical(g0)
    c: Coincident(g1,g0)
    c: Horizontal(g1)
    c: DistanceY(g0,g-1) = 53
    c: DistanceX(g0,g-1) = 53
    c: Vertical(g2)
    c: Coincident(g3,g2)
    c: Horizontal(g3)
    c: DistanceY(g0,g2) = 5
    c: DistanceX(g0,g2) = 5
    c: Coincident(g4,g2)
    c: Horizontal(g4)
    c: Vertical(g5)
    c: Coincident(g0,g4)
    c: Coincident(g1,g5)
    c: Equal(g0,g1)
    c: Equal(g2,g3)
    c: Equal(g4,g5)
    c: DistanceY(g0,g0) = 18
FEATURE [PartDesign::Pad] Pad012
  Direction = (1,1,1)
  Length = 100
  Length2 = 100
  Profile = -> Sketch032
  Type = 0
FEATURE [Sketcher::SketchObject] Sketch034
  ExternalGeometry = -> [Pad012]
  FullyConstrained = true
  MapMode = 5
  Placement = pos=(0,0,100) rot=(0,0,1;0rad)
  Support = -> [Pad012]
  sketch-geometry (6):
    g0: LineSegment StartX=-53 StartY=-35 StartZ=0 EndX=-53 EndY=-53 EndZ=0
    g1: LineSegment StartX=-53 StartY=-53 StartZ=0 EndX=-35 EndY=-53 EndZ=0
    g2: LineSegment StartX=-35 StartY=-53 StartZ=0 EndX=-35 EndY=-50 EndZ=0
    g3: LineSegment StartX=-35 StartY=-50 StartZ=0 EndX=-50 EndY=-50 EndZ=0
    g4: LineSegment StartX=-50 StartY=-50 StartZ=0 EndX=-50 EndY=-35 EndZ=0
    g5: LineSegment StartX=-50 StartY=-35 StartZ=0 EndX=-53 EndY=-35 EndZ=0
  constraints (15):
    c: Coincident(g-5,g0)
    c: Coincident(g0,g-4)
    c: Coincident(g0,g1)
    c: Coincident(g1,g-6)
    c: Coincident(g1,g2)
    c: PointOnObject(g2,g-6)
    c: Coincident(g2,g3)
    c: Horizontal(g3)
    c: Coincident(g3,g4)
    c: PointOnObject(g4,g-5)
    c: Vertical(g4)
    c: Coincident(g4,g5)
    c: Coincident(g5,g0)
    c: Equal(g5,g2)
    c: DistanceX(g5,g5) = 3
FEATURE [PartDesign::Pad] Pad015
  BaseFeature = -> Pad012
  Direction = (1,1,1)
  Length = 10
  Length2 = 100
  Profile = -> Sketch034
  Type = 0
FEATURE [Sketcher::SketchObject] Sketch035
  ExternalGeometry = -> [Pad015]
  FullyConstrained = true
  MapMode = 5
  Placement = pos=(0,-53,0) rot=(1,0,0;1.5708rad)
  Support = -> [Pad015]
  sketch-geometry (1):
    g0: Circle CenterX=-43 CenterY=105 CenterZ=0 NormalX=0 NormalY=0 NormalZ=1 AngleXU=0 Radius=1.6
  constraints (3):
    c: Radius(g0) = 1.6
    c: DistanceX(g-3,g0) = 10
    c: DistanceY(g0,g-3) = 5
FEATURE [PartDesign::Pocket] Pocket023
  BaseFeature = -> Pad015
  Length = 5
  Length2 = 100
  Profile = -> Sketch035
  Type = 0
FEATURE [Sketcher::SketchObject] Sketch036
  ExternalGeometry = -> [Pocket023]
  FullyConstrained = true
  MapMode = 5
  Placement = pos=(0,-53,0) rot=(1,0,0;1.5708rad)
  Support = -> [Pocket023]
  sketch-geometry (1):
    g0: Circle CenterX=-43 CenterY=105 CenterZ=0 NormalX=0 NormalY=0 NormalZ=1 AngleXU=0 Radius=3.5
  constraints (2):
    c: Coincident(g0,g-3)
    c: Radius(g0) = 3.5
FEATURE [PartDesign::Pocket] Pocket019
  BaseFeature = -> Pocket023
  Length = 1
  Length2 = 100
  Profile = -> Sketch036
  Type = 0
FEATURE [Sketcher::SketchObject] Sketch037
  ExternalGeometry = -> [Pocket019]
  FullyConstrained = true
  MapMode = 5
  Placement = pos=(-53,0,0) rot=(0.57735,-0.57735,-0.57735;2.0944rad)
  Support = -> [Pocket019]
  sketch-geometry (1):
    g0: Circle CenterX=43 CenterY=105 CenterZ=0 NormalX=0 NormalY=0 NormalZ=1 AngleXU=0 Radius=1.75
  constraints (3):
    c: Radius(g0) = 1.75
    c: DistanceX(g0,g-3) = 10
    c: DistanceY(g0,g-3) = 5
FEATURE [PartDesign::Pocket] Pocket020
  BaseFeature = -> Pocket019
  Length = 5
  Length2 = 100
  Profile = -> Sketch037
  Type = 0
FEATURE [Sketcher::SketchObject] Sketch038
  ExternalGeometry = -> [Pocket020]
  FullyConstrained = true
  MapMode = 5
  Placement = pos=(-53,0,0) rot=(0.57735,-0.57735,-0.57735;2.0944rad)
  Support = -> [Pocket020]
  sketch-geometry (1):
    g0: Circle CenterX=43 CenterY=105 CenterZ=0 NormalX=0 NormalY=0 NormalZ=1 AngleXU=0 Radius=3.5
  constraints (2):
    c: Coincident(g0,g-3)
    c: Radius(g0) = 3.5
FEATURE [PartDesign::Pocket] Pocket021
  BaseFeature = -> Pocket020
  Length = 1
  Length2 = 100
  Profile = -> Sketch038
  Type = 0
FEATURE [Sketcher::SketchObject] Sketch033
  ExternalGeometry = -> [Pocket021]
  FullyConstrained = true
  MapMode = 5
  Placement = pos=(0,0,0) rot=(1,0,0;3.14159rad)
  Support = -> [Pocket021]
  sketch-geometry (6):
    g0: LineSegment StartX=-35 StartY=53 StartZ=0 EndX=-53 EndY=53 EndZ=0
    g1: LineSegment StartX=-53 StartY=53 StartZ=0 EndX=-53 EndY=35 EndZ=0
    g2: LineSegment StartX=-53 StartY=35 StartZ=0 EndX=-50 EndY=35 EndZ=0
    g3: LineSegment StartX=-50 StartY=35 StartZ=0 EndX=-50 EndY=50 EndZ=0
    g4: LineSegment StartX=-50 StartY=50 StartZ=0 EndX=-35 EndY=50 EndZ=0
    g5: LineSegment StartX=-35 StartY=50 StartZ=0 EndX=-35 EndY=53 EndZ=0
  constraints (15):
    c: Coincident(g-6,g0)
    c: Coincident(g0,g-4)
    c: Coincident(g0,g1)
    c: Coincident(g1,g-5)
    c: Coincident(g1,g2)
    c: PointOnObject(g2,g-5)
    c: Coincident(g2,g3)
    c: Vertical(g3)
    c: Coincident(g3,g4)
    c: PointOnObject(g4,g-6)
    c: Horizontal(g4)
    c: Coincident(g4,g5)
    c: Coincident(g5,g0)
    c: Equal(g5,g2)
    c: DistanceY(g5,g5) = 3
FEATURE [PartDesign::Pad] Pad013
  BaseFeature = -> Pocket021
  Direction = (1,1,1)
  Length = 40
  Length2 = 100
  Profile = -> Sketch033
  Type = 0
FEATURE [Sketcher::SketchObject] Sketch039
  ExternalGeometry = -> [Pad013]
  FullyConstrained = true
  MapMode = 5
  Placement = pos=(0,0,-40) rot=(1,0,0;3.14159rad)
  Support = -> [Pad013]
  sketch-geometry (5):
    g0: LineSegment StartX=-35 StartY=50 StartZ=0 EndX=-35 EndY=53 EndZ=0
    g1: LineSegment StartX=-35 StartY=53 StartZ=0 EndX=-53 EndY=53 EndZ=0
    g2: LineSegment StartX=-53 StartY=53 StartZ=0 EndX=-53 EndY=35 EndZ=0
    g3: LineSegment StartX=-53 StartY=35 StartZ=0 EndX=-50 EndY=35 EndZ=0
    g4: LineSegment StartX=-50 StartY=35 StartZ=0 EndX=-35 EndY=50 EndZ=0
  constraints (10):
    c: Coincident(g-5,g0)
    c: Coincident(g0,g-5)
    c: Coincident(g0,g1)
    c: Coincident(g1,g-4)
    c: Coincident(g1,g2)
    c: Coincident(g2,g-6)
    c: Coincident(g2,g3)
    c: Coincident(g3,g-6)
    c: Coincident(g3,g4)
    c: Coincident(g4,g0)
FEATURE [PartDesign::Pad] Pad014
  BaseFeature = -> Pad013
  Direction = (1,1,1)
  Length = 3
  Length2 = 100
  Profile = -> Sketch039
  Type = 0
FEATURE [Sketcher::SketchObject] Sketch031
  ExternalGeometry = -> [Pad014]
  FullyConstrained = true
  MapMode = 5
  Placement = pos=(-53,0,0) rot=(0.57735,-0.57735,-0.57735;2.0944rad)
  Support = -> [Pad014]
  sketch-geometry (1):
    g0: Circle CenterX=43 CenterY=-5 CenterZ=0 NormalX=0 NormalY=0 NormalZ=1 AngleXU=0 Radius=1.75
  constraints (3):
    c: Radius(g0) = 1.75
    c: DistanceY(g0,g-4) = 5
    c: DistanceX(g0,g-4) = 10
FEATURE [PartDesign::Pocket] Pocket022
  BaseFeature = -> Pad014
  Length = 5
  Length2 = 100
  Profile = -> Sketch031
  Type = 0
FEATURE [Sketcher::SketchObject] Sketch042
  ExternalGeometry = -> [Pocket022]
  FullyConstrained = true
  MapMode = 5
  Placement = pos=(-53,0,0) rot=(0.57735,-0.57735,-0.57735;2.0944rad)
  Support = -> [Pocket022]
  sketch-geometry (1):
    g0: Circle CenterX=43 CenterY=-5 CenterZ=0 NormalX=0 NormalY=0 NormalZ=1 AngleXU=0 Radius=3.5
  constraints (2):
    c: Coincident(g0,g-3)
    c: Radius(g0) = 3.5
FEATURE [PartDesign::Pocket] Pocket026
  BaseFeature = -> Pocket022
  Length = 1
  Length2 = 100
  Profile = -> Sketch042
  Type = 0
FEATURE [Sketcher::SketchObject] Sketch040
  ExternalGeometry = -> [Pocket026]
  FullyConstrained = true
  MapMode = 5
  Placement = pos=(0,-53,0) rot=(1,0,0;1.5708rad)
  Support = -> [Pocket026]
  sketch-geometry (1):
    g0: Circle CenterX=-43 CenterY=-5 CenterZ=0 NormalX=0 NormalY=0 NormalZ=1 AngleXU=0 Radius=1.75
  constraints (3):
    c: DistanceX(g-3,g0) = 10
    c: DistanceY(g0,g-4) = 5
    c: Radius(g0) = 1.75
FEATURE [PartDesign::Pocket] Pocket024
  BaseFeature = -> Pocket026
  Length = 5
  Length2 = 100
  Profile = -> Sketch040
  Type = 0
FEATURE [Sketcher::SketchObject] Sketch041
  ExternalGeometry = -> [Pocket024]
  FullyConstrained = true
  MapMode = 5
  Placement = pos=(0,-53,0) rot=(1,0,0;1.5708rad)
  Support = -> [Pocket024]
  sketch-geometry (1):
    g0: Circle CenterX=-43 CenterY=-5 CenterZ=0 NormalX=0 NormalY=0 NormalZ=1 AngleXU=0 Radius=3.5
  constraints (2):
    c: Coincident(g0,g-3)
    c: Radius(g0) = 3.5
FEATURE [PartDesign::Pocket] Pocket025
  BaseFeature = -> Pocket024
  Length = 1
  Length2 = 100
  Profile = -> Sketch041
  Type = 0
FEATURE [PartDesign::Body] Body005  label="side_frame001"
  Group = -> [Sketch032,Pad012,Sketch034,Pad015,Sketch035,Pocket023,Sketch036,Pocket019,Sketch037,Pocket020,Sketch038,Pocket021,Sketch033,Pad013,Sketch039,Pad014,Sketch031,Pocket022,Sketch042,Pocket026,Sketch040,Pocket024,Sketch041,Pocket025]
  Origin = -> Origin005
  Placement = pos=(0,0,0) rot=(0,0,1;1.5708rad)
  Tip = -> Pocket025
FEATURE [Sketcher::SketchObject] Sketch044
  FullyConstrained = true
  MapMode = 5
  Support = -> [XY_Plane006]
  sketch-geometry (6):
    g0: LineSegment StartX=-53 StartY=-35 StartZ=0 EndX=-53 EndY=-53 EndZ=0
    g1: LineSegment StartX=-53 StartY=-53 StartZ=0 EndX=-35 EndY=-53 EndZ=0
    g2: LineSegment StartX=-48 StartY=-35 StartZ=0 EndX=-48 EndY=-48 EndZ=0
    g3: LineSegment StartX=-48 StartY=-48 StartZ=0 EndX=-35 EndY=-48 EndZ=0
    g4: LineSegment StartX=-48 StartY=-35 StartZ=0 EndX=-53 EndY=-35 EndZ=0
    g5: LineSegment StartX=-35 StartY=-48 StartZ=0 EndX=-35 EndY=-53 EndZ=0
  constraints (19):
    c: Vertical(g0)
    c: Coincident(g1,g0)
    c: Horizontal(g1)
    c: DistanceY(g0,g-1) = 53
    c: DistanceX(g0,g-1) = 53
    c: Vertical(g2)
    c: Coincident(g3,g2)
    c: Horizontal(g3)
    c: DistanceY(g0,g2) = 5
    c: DistanceX(g0,g2) = 5
    c: Coincident(g4,g2)
    c: Horizontal(g4)
    c: Vertical(g5)
    c: Coincident(g0,g4)
    c: Coincident(g1,g5)
    c: Equal(g0,g1)
    c: Equal(g2,g3)
    c: Equal(g4,g5)
    c: DistanceY(g0,g0) = 18
FEATURE [PartDesign::Pad] Pad016
  Direction = (1,1,1)
  Length = 100
  Length2 = 100
  Profile = -> Sketch044
  Type = 0
FEATURE [Sketcher::SketchObject] Sketch046
  ExternalGeometry = -> [Pad016]
  FullyConstrained = true
  MapMode = 5
  Placement = pos=(0,0,100) rot=(0,0,1;0rad)
  Support = -> [Pad016]
  sketch-geometry (6):
    g0: LineSegment StartX=-53 StartY=-35 StartZ=0 EndX=-53 EndY=-53 EndZ=0
    g1: LineSegment StartX=-53 StartY=-53 StartZ=0 EndX=-35 EndY=-53 EndZ=0
    g2: LineSegment StartX=-35 StartY=-53 StartZ=0 EndX=-35 EndY=-50 EndZ=0
    g3: LineSegment StartX=-35 StartY=-50 StartZ=0 EndX=-50 EndY=-50 EndZ=0
    g4: LineSegment StartX=-50 StartY=-50 StartZ=0 EndX=-50 EndY=-35 EndZ=0
    g5: LineSegment StartX=-50 StartY=-35 StartZ=0 EndX=-53 EndY=-35 EndZ=0
  constraints (15):
    c: Coincident(g-5,g0)
    c: Coincident(g0,g-4)
    c: Coincident(g0,g1)
    c: Coincident(g1,g-6)
    c: Coincident(g1,g2)
    c: PointOnObject(g2,g-6)
    c: Coincident(g2,g3)
    c: Horizontal(g3)
    c: Coincident(g3,g4)
    c: PointOnObject(g4,g-5)
    c: Vertical(g4)
    c: Coincident(g4,g5)
    c: Coincident(g5,g0)
    c: Equal(g5,g2)
    c: DistanceX(g5,g5) = 3
FEATURE [PartDesign::Pad] Pad019
  BaseFeature = -> Pad016
  Direction = (1,1,1)
  Length = 10
  Length2 = 100
  Profile = -> Sketch046
  Type = 0
FEATURE [Sketcher::SketchObject] Sketch047
  ExternalGeometry = -> [Pad019]
  FullyConstrained = true
  MapMode = 5
  Placement = pos=(0,-53,0) rot=(1,0,0;1.5708rad)
  Support = -> [Pad019]
  sketch-geometry (1):
    g0: Circle CenterX=-43 CenterY=105 CenterZ=0 NormalX=0 NormalY=0 NormalZ=1 AngleXU=0 Radius=1.6
  constraints (3):
    c: Radius(g0) = 1.6
    c: DistanceX(g-3,g0) = 10
    c: DistanceY(g0,g-3) = 5
FEATURE [PartDesign::Pocket] Pocket031
  BaseFeature = -> Pad019
  Length = 5
  Length2 = 100
  Profile = -> Sketch047
  Type = 0
FEATURE [Sketcher::SketchObject] Sketch048
  ExternalGeometry = -> [Pocket031]
  FullyConstrained = true
  MapMode = 5
  Placement = pos=(0,-53,0) rot=(1,0,0;1.5708rad)
  Support = -> [Pocket031]
  sketch-geometry (1):
    g0: Circle CenterX=-43 CenterY=105 CenterZ=0 NormalX=0 NormalY=0 NormalZ=1 AngleXU=0 Radius=3.5
  constraints (2):
    c: Coincident(g0,g-3)
    c: Radius(g0) = 3.5
FEATURE [PartDesign::Pocket] Pocket027
  BaseFeature = -> Pocket031
  Length = 1
  Length2 = 100
  Profile = -> Sketch048
  Type = 0
FEATURE [Sketcher::SketchObject] Sketch049
  ExternalGeometry = -> [Pocket027]
  FullyConstrained = true
  MapMode = 5
  Placement = pos=(-53,0,0) rot=(0.57735,-0.57735,-0.57735;2.0944rad)
  Support = -> [Pocket027]
  sketch-geometry (1):
    g0: Circle CenterX=43 CenterY=105 CenterZ=0 NormalX=0 NormalY=0 NormalZ=1 AngleXU=0 Radius=1.75
  constraints (3):
    c: Radius(g0) = 1.75
    c: DistanceX(g0,g-3) = 10
    c: DistanceY(g0,g-3) = 5
FEATURE [PartDesign::Pocket] Pocket028
  BaseFeature = -> Pocket027
  Length = 5
  Length2 = 100
  Profile = -> Sketch049
  Type = 0
FEATURE [Sketcher::SketchObject] Sketch050
  ExternalGeometry = -> [Pocket028]
  FullyConstrained = true
  MapMode = 5
  Placement = pos=(-53,0,0) rot=(0.57735,-0.57735,-0.57735;2.0944rad)
  Support = -> [Pocket028]
  sketch-geometry (1):
    g0: Circle CenterX=43 CenterY=105 CenterZ=0 NormalX=0 NormalY=0 NormalZ=1 AngleXU=0 Radius=3.5
  constraints (2):
    c: Coincident(g0,g-3)
    c: Radius(g0) = 3.5
FEATURE [PartDesign::Pocket] Pocket029
  BaseFeature = -> Pocket028
  Length = 1
  Length2 = 100
  Profile = -> Sketch050
  Type = 0
FEATURE [Sketcher::SketchObject] Sketch045
  ExternalGeometry = -> [Pocket029]
  FullyConstrained = true
  MapMode = 5
  Placement = pos=(0,0,0) rot=(1,0,0;3.14159rad)
  Support = -> [Pocket029]
  sketch-geometry (6):
    g0: LineSegment StartX=-35 StartY=53 StartZ=0 EndX=-53 EndY=53 EndZ=0
    g1: LineSegment StartX=-53 StartY=53 StartZ=0 EndX=-53 EndY=35 EndZ=0
    g2: LineSegment StartX=-53 StartY=35 StartZ=0 EndX=-50 EndY=35 EndZ=0
    g3: LineSegment StartX=-50 StartY=35 StartZ=0 EndX=-50 EndY=50 EndZ=0
    g4: LineSegment StartX=-50 StartY=50 StartZ=0 EndX=-35 EndY=50 EndZ=0
    g5: LineSegment StartX=-35 StartY=50 StartZ=0 EndX=-35 EndY=53 EndZ=0
  constraints (15):
    c: Coincident(g-6,g0)
    c: Coincident(g0,g-4)
    c: Coincident(g0,g1)
    c: Coincident(g1,g-5)
    c: Coincident(g1,g2)
    c: PointOnObject(g2,g-5)
    c: Coincident(g2,g3)
    c: Vertical(g3)
    c: Coincident(g3,g4)
    c: PointOnObject(g4,g-6)
    c: Horizontal(g4)
    c: Coincident(g4,g5)
    c: Coincident(g5,g0)
    c: Equal(g5,g2)
    c: DistanceY(g5,g5) = 3
FEATURE [PartDesign::Pad] Pad017
  BaseFeature = -> Pocket029
  Direction = (1,1,1)
  Length = 40
  Length2 = 100
  Profile = -> Sketch045
  Type = 0
FEATURE [Sketcher::SketchObject] Sketch051
  ExternalGeometry = -> [Pad017]
  FullyConstrained = true
  MapMode = 5
  Placement = pos=(0,0,-40) rot=(1,0,0;3.14159rad)
  Support = -> [Pad017]
  sketch-geometry (5):
    g0: LineSegment StartX=-35 StartY=50 StartZ=0 EndX=-35 EndY=53 EndZ=0
    g1: LineSegment StartX=-35 StartY=53 StartZ=0 EndX=-53 EndY=53 EndZ=0
    g2: LineSegment StartX=-53 StartY=53 StartZ=0 EndX=-53 EndY=35 EndZ=0
    g3: LineSegment StartX=-53 StartY=35 StartZ=0 EndX=-50 EndY=35 EndZ=0
    g4: LineSegment StartX=-50 StartY=35 StartZ=0 EndX=-35 EndY=50 EndZ=0
  constraints (10):
    c: Coincident(g-5,g0)
    c: Coincident(g0,g-5)
    c: Coincident(g0,g1)
    c: Coincident(g1,g-4)
    c: Coincident(g1,g2)
    c: Coincident(g2,g-6)
    c: Coincident(g2,g3)
    c: Coincident(g3,g-6)
    c: Coincident(g3,g4)
    c: Coincident(g4,g0)
FEATURE [PartDesign::Pad] Pad018
  BaseFeature = -> Pad017
  Direction = (1,1,1)
  Length = 3
  Length2 = 100
  Profile = -> Sketch051
  Type = 0
FEATURE [Sketcher::SketchObject] Sketch043
  ExternalGeometry = -> [Pad018]
  FullyConstrained = true
  MapMode = 5
  Placement = pos=(-53,0,0) rot=(0.57735,-0.57735,-0.57735;2.0944rad)
  Support = -> [Pad018]
  sketch-geometry (1):
    g0: Circle CenterX=43 CenterY=-5 CenterZ=0 NormalX=0 NormalY=0 NormalZ=1 AngleXU=0 Radius=1.75
  constraints (3):
    c: Radius(g0) = 1.75
    c: DistanceY(g0,g-4) = 5
    c: DistanceX(g0,g-4) = 10
FEATURE [PartDesign::Pocket] Pocket030
  BaseFeature = -> Pad018
  Length = 5
  Length2 = 100
  Profile = -> Sketch043
  Type = 0
FEATURE [Sketcher::SketchObject] Sketch054
  ExternalGeometry = -> [Pocket030]
  FullyConstrained = true
  MapMode = 5
  Placement = pos=(-53,0,0) rot=(0.57735,-0.57735,-0.57735;2.0944rad)
  Support = -> [Pocket030]
  sketch-geometry (1):
    g0: Circle CenterX=43 CenterY=-5 CenterZ=0 NormalX=0 NormalY=0 NormalZ=1 AngleXU=0 Radius=3.5
  constraints (2):
    c: Coincident(g0,g-3)
    c: Radius(g0) = 3.5
FEATURE [PartDesign::Pocket] Pocket034
  BaseFeature = -> Pocket030
  Length = 1
  Length2 = 100
  Profile = -> Sketch054
  Type = 0
FEATURE [Sketcher::SketchObject] Sketch052
  ExternalGeometry = -> [Pocket034]
  FullyConstrained = true
  MapMode = 5
  Placement = pos=(0,-53,0) rot=(1,0,0;1.5708rad)
  Support = -> [Pocket034]
  sketch-geometry (1):
    g0: Circle CenterX=-43 CenterY=-5 CenterZ=0 NormalX=0 NormalY=0 NormalZ=1 AngleXU=0 Radius=1.75
  constraints (3):
    c: DistanceX(g-3,g0) = 10
    c: DistanceY(g0,g-4) = 5
    c: Radius(g0) = 1.75
FEATURE [PartDesign::Pocket] Pocket032
  BaseFeature = -> Pocket034
  Length = 5
  Length2 = 100
  Profile = -> Sketch052
  Type = 0
FEATURE [Sketcher::SketchObject] Sketch053
  ExternalGeometry = -> [Pocket032]
  FullyConstrained = true
  MapMode = 5
  Placement = pos=(0,-53,0) rot=(1,0,0;1.5708rad)
  Support = -> [Pocket032]
  sketch-geometry (1):
    g0: Circle CenterX=-43 CenterY=-5 CenterZ=0 NormalX=0 NormalY=0 NormalZ=1 AngleXU=0 Radius=3.5
  constraints (2):
    c: Coincident(g0,g-3)
    c: Radius(g0) = 3.5
FEATURE [PartDesign::Pocket] Pocket033
  BaseFeature = -> Pocket032
  Length = 1
  Length2 = 100
  Profile = -> Sketch053
  Type = 0
FEATURE [PartDesign::Body] Body006  label="side_frame002"
  Group = -> [Sketch044,Pad016,Sketch046,Pad019,Sketch047,Pocket031,Sketch048,Pocket027,Sketch049,Pocket028,Sketch050,Pocket029,Sketch045,Pad017,Sketch051,Pad018,Sketch043,Pocket030,Sketch054,Pocket034,Sketch052,Pocket032,Sketch053,Pocket033]
  Origin = -> Origin006
  Placement = pos=(0,0,0) rot=(0,0,1;3.14159rad)
  Tip = -> Pocket033
FEATURE [Sketcher::SketchObject] Sketch056
  FullyConstrained = true
  MapMode = 5
  Support = -> [XY_Plane007]
  sketch-geometry (6):
    g0: LineSegment StartX=-53 StartY=-35 StartZ=0 EndX=-53 EndY=-53 EndZ=0
    g1: LineSegment StartX=-53 StartY=-53 StartZ=0 EndX=-35 EndY=-53 EndZ=0
    g2: LineSegment StartX=-48 StartY=-35 StartZ=0 EndX=-48 EndY=-48 EndZ=0
    g3: LineSegment StartX=-48 StartY=-48 StartZ=0 EndX=-35 EndY=-48 EndZ=0
    g4: LineSegment StartX=-48 StartY=-35 StartZ=0 EndX=-53 EndY=-35 EndZ=0
    g5: LineSegment StartX=-35 StartY=-48 StartZ=0 EndX=-35 EndY=-53 EndZ=0
  constraints (19):
    c: Vertical(g0)
    c: Coincident(g1,g0)
    c: Horizontal(g1)
    c: DistanceY(g0,g-1) = 53
    c: DistanceX(g0,g-1) = 53
    c: Vertical(g2)
    c: Coincident(g3,g2)
    c: Horizontal(g3)
    c: DistanceY(g0,g2) = 5
    c: DistanceX(g0,g2) = 5
    c: Coincident(g4,g2)
    c: Horizontal(g4)
    c: Vertical(g5)
    c: Coincident(g0,g4)
    c: Coincident(g1,g5)
    c: Equal(g0,g1)
    c: Equal(g2,g3)
    c: Equal(g4,g5)
    c: DistanceY(g0,g0) = 18
FEATURE [PartDesign::Pad] Pad020
  Direction = (1,1,1)
  Length = 100
  Length2 = 100
  Profile = -> Sketch056
  Type = 0
FEATURE [Sketcher::SketchObject] Sketch058
  ExternalGeometry = -> [Pad020]
  FullyConstrained = true
  MapMode = 5
  Placement = pos=(0,0,100) rot=(0,0,1;0rad)
  Support = -> [Pad020]
  sketch-geometry (6):
    g0: LineSegment StartX=-53 StartY=-35 StartZ=0 EndX=-53 EndY=-53 EndZ=0
    g1: LineSegment StartX=-53 StartY=-53 StartZ=0 EndX=-35 EndY=-53 EndZ=0
    g2: LineSegment StartX=-35 StartY=-53 StartZ=0 EndX=-35 EndY=-50 EndZ=0
    g3: LineSegment StartX=-35 StartY=-50 StartZ=0 EndX=-50 EndY=-50 EndZ=0
    g4: LineSegment StartX=-50 StartY=-50 StartZ=0 EndX=-50 EndY=-35 EndZ=0
    g5: LineSegment StartX=-50 StartY=-35 StartZ=0 EndX=-53 EndY=-35 EndZ=0
  constraints (15):
    c: Coincident(g-5,g0)
    c: Coincident(g0,g-4)
    c: Coincident(g0,g1)
    c: Coincident(g1,g-6)
    c: Coincident(g1,g2)
    c: PointOnObject(g2,g-6)
    c: Coincident(g2,g3)
    c: Horizontal(g3)
    c: Coincident(g3,g4)
    c: PointOnObject(g4,g-5)
    c: Vertical(g4)
    c: Coincident(g4,g5)
    c: Coincident(g5,g0)
    c: Equal(g5,g2)
    c: DistanceX(g5,g5) = 3
FEATURE [PartDesign::Pad] Pad023
  BaseFeature = -> Pad020
  Direction = (1,1,1)
  Length = 10
  Length2 = 100
  Profile = -> Sketch058
  Type = 0
FEATURE [Sketcher::SketchObject] Sketch059
  ExternalGeometry = -> [Pad023]
  FullyConstrained = true
  MapMode = 5
  Placement = pos=(0,-53,0) rot=(1,0,0;1.5708rad)
  Support = -> [Pad023]
  sketch-geometry (1):
    g0: Circle CenterX=-43 CenterY=105 CenterZ=0 NormalX=0 NormalY=0 NormalZ=1 AngleXU=0 Radius=1.6
  constraints (3):
    c: Radius(g0) = 1.6
    c: DistanceX(g-3,g0) = 10
    c: DistanceY(g0,g-3) = 5
FEATURE [PartDesign::Pocket] Pocket039
  BaseFeature = -> Pad023
  Length = 5
  Length2 = 100
  Profile = -> Sketch059
  Type = 0
FEATURE [Sketcher::SketchObject] Sketch060
  ExternalGeometry = -> [Pocket039]
  FullyConstrained = true
  MapMode = 5
  Placement = pos=(0,-53,0) rot=(1,0,0;1.5708rad)
  Support = -> [Pocket039]
  sketch-geometry (1):
    g0: Circle CenterX=-43 CenterY=105 CenterZ=0 NormalX=0 NormalY=0 NormalZ=1 AngleXU=0 Radius=3.5
  constraints (2):
    c: Coincident(g0,g-3)
    c: Radius(g0) = 3.5
FEATURE [PartDesign::Pocket] Pocket035
  BaseFeature = -> Pocket039
  Length = 1
  Length2 = 100
  Profile = -> Sketch060
  Type = 0
FEATURE [Sketcher::SketchObject] Sketch061
  ExternalGeometry = -> [Pocket035]
  FullyConstrained = true
  MapMode = 5
  Placement = pos=(-53,0,0) rot=(0.57735,-0.57735,-0.57735;2.0944rad)
  Support = -> [Pocket035]
  sketch-geometry (1):
    g0: Circle CenterX=43 CenterY=105 CenterZ=0 NormalX=0 NormalY=0 NormalZ=1 AngleXU=0 Radius=1.75
  constraints (3):
    c: Radius(g0) = 1.75
    c: DistanceX(g0,g-3) = 10
    c: DistanceY(g0,g-3) = 5
FEATURE [PartDesign::Pocket] Pocket036
  BaseFeature = -> Pocket035
  Length = 5
  Length2 = 100
  Profile = -> Sketch061
  Type = 0
FEATURE [Sketcher::SketchObject] Sketch062
  ExternalGeometry = -> [Pocket036]
  FullyConstrained = true
  MapMode = 5
  Placement = pos=(-53,0,0) rot=(0.57735,-0.57735,-0.57735;2.0944rad)
  Support = -> [Pocket036]
  sketch-geometry (1):
    g0: Circle CenterX=43 CenterY=105 CenterZ=0 NormalX=0 NormalY=0 NormalZ=1 AngleXU=0 Radius=3.5
  constraints (2):
    c: Coincident(g0,g-3)
    c: Radius(g0) = 3.5
FEATURE [PartDesign::Pocket] Pocket037
  BaseFeature = -> Pocket036
  Length = 1
  Length2 = 100
  Profile = -> Sketch062
  Type = 0
FEATURE [Sketcher::SketchObject] Sketch057
  ExternalGeometry = -> [Pocket037]
  FullyConstrained = true
  MapMode = 5
  Placement = pos=(0,0,0) rot=(1,0,0;3.14159rad)
  Support = -> [Pocket037]
  sketch-geometry (6):
    g0: LineSegment StartX=-35 StartY=53 StartZ=0 EndX=-53 EndY=53 EndZ=0
    g1: LineSegment StartX=-53 StartY=53 StartZ=0 EndX=-53 EndY=35 EndZ=0
    g2: LineSegment StartX=-53 StartY=35 StartZ=0 EndX=-50 EndY=35 EndZ=0
    g3: LineSegment StartX=-50 StartY=35 StartZ=0 EndX=-50 EndY=50 EndZ=0
    g4: LineSegment StartX=-50 StartY=50 StartZ=0 EndX=-35 EndY=50 EndZ=0
    g5: LineSegment StartX=-35 StartY=50 StartZ=0 EndX=-35 EndY=53 EndZ=0
  constraints (15):
    c: Coincident(g-6,g0)
    c: Coincident(g0,g-4)
    c: Coincident(g0,g1)
    c: Coincident(g1,g-5)
    c: Coincident(g1,g2)
    c: PointOnObject(g2,g-5)
    c: Coincident(g2,g3)
    c: Vertical(g3)
    c: Coincident(g3,g4)
    c: PointOnObject(g4,g-6)
    c: Horizontal(g4)
    c: Coincident(g4,g5)
    c: Coincident(g5,g0)
    c: Equal(g5,g2)
    c: DistanceY(g5,g5) = 3
FEATURE [PartDesign::Pad] Pad021
  BaseFeature = -> Pocket037
  Direction = (1,1,1)
  Length = 40
  Length2 = 100
  Profile = -> Sketch057
  Type = 0
FEATURE [Sketcher::SketchObject] Sketch063
  ExternalGeometry = -> [Pad021]
  FullyConstrained = true
  MapMode = 5
  Placement = pos=(0,0,-40) rot=(1,0,0;3.14159rad)
  Support = -> [Pad021]
  sketch-geometry (5):
    g0: LineSegment StartX=-35 StartY=50 StartZ=0 EndX=-35 EndY=53 EndZ=0
    g1: LineSegment StartX=-35 StartY=53 StartZ=0 EndX=-53 EndY=53 EndZ=0
    g2: LineSegment StartX=-53 StartY=53 StartZ=0 EndX=-53 EndY=35 EndZ=0
    g3: LineSegment StartX=-53 StartY=35 StartZ=0 EndX=-50 EndY=35 EndZ=0
    g4: LineSegment StartX=-50 StartY=35 StartZ=0 EndX=-35 EndY=50 EndZ=0
  constraints (10):
    c: Coincident(g-5,g0)
    c: Coincident(g0,g-5)
    c: Coincident(g0,g1)
    c: Coincident(g1,g-4)
    c: Coincident(g1,g2)
    c: Coincident(g2,g-6)
    c: Coincident(g2,g3)
    c: Coincident(g3,g-6)
    c: Coincident(g3,g4)
    c: Coincident(g4,g0)
FEATURE [PartDesign::Pad] Pad022
  BaseFeature = -> Pad021
  Direction = (1,1,1)
  Length = 3
  Length2 = 100
  Profile = -> Sketch063
  Type = 0
FEATURE [Sketcher::SketchObject] Sketch055
  ExternalGeometry = -> [Pad022]
  FullyConstrained = true
  MapMode = 5
  Placement = pos=(-53,0,0) rot=(0.57735,-0.57735,-0.57735;2.0944rad)
  Support = -> [Pad022]
  sketch-geometry (1):
    g0: Circle CenterX=43 CenterY=-5 CenterZ=0 NormalX=0 NormalY=0 NormalZ=1 AngleXU=0 Radius=1.75
  constraints (3):
    c: Radius(g0) = 1.75
    c: DistanceY(g0,g-4) = 5
    c: DistanceX(g0,g-4) = 10
FEATURE [PartDesign::Pocket] Pocket038
  BaseFeature = -> Pad022
  Length = 5
  Length2 = 100
  Profile = -> Sketch055
  Type = 0
FEATURE [Sketcher::SketchObject] Sketch066
  ExternalGeometry = -> [Pocket038]
  FullyConstrained = true
  MapMode = 5
  Placement = pos=(-53,0,0) rot=(0.57735,-0.57735,-0.57735;2.0944rad)
  Support = -> [Pocket038]
  sketch-geometry (1):
    g0: Circle CenterX=43 CenterY=-5 CenterZ=0 NormalX=0 NormalY=0 NormalZ=1 AngleXU=0 Radius=3.5
  constraints (2):
    c: Coincident(g0,g-3)
    c: Radius(g0) = 3.5
FEATURE [PartDesign::Pocket] Pocket042
  BaseFeature = -> Pocket038
  Length = 1
  Length2 = 100
  Profile = -> Sketch066
  Type = 0
FEATURE [Sketcher::SketchObject] Sketch064
  ExternalGeometry = -> [Pocket042]
  FullyConstrained = true
  MapMode = 5
  Placement = pos=(0,-53,0) rot=(1,0,0;1.5708rad)
  Support = -> [Pocket042]
  sketch-geometry (1):
    g0: Circle CenterX=-43 CenterY=-5 CenterZ=0 NormalX=0 NormalY=0 NormalZ=1 AngleXU=0 Radius=1.75
  constraints (3):
    c: DistanceX(g-3,g0) = 10
    c: DistanceY(g0,g-4) = 5
    c: Radius(g0) = 1.75
FEATURE [PartDesign::Pocket] Pocket040
  BaseFeature = -> Pocket042
  Length = 5
  Length2 = 100
  Profile = -> Sketch064
  Type = 0
FEATURE [Sketcher::SketchObject] Sketch065
  ExternalGeometry = -> [Pocket040]
  FullyConstrained = true
  MapMode = 5
  Placement = pos=(0,-53,0) rot=(1,0,0;1.5708rad)
  Support = -> [Pocket040]
  sketch-geometry (1):
    g0: Circle CenterX=-43 CenterY=-5 CenterZ=0 NormalX=0 NormalY=0 NormalZ=1 AngleXU=0 Radius=3.5
  constraints (2):
    c: Coincident(g0,g-3)
    c: Radius(g0) = 3.5
FEATURE [PartDesign::Pocket] Pocket041
  BaseFeature = -> Pocket040
  Length = 1
  Length2 = 100
  Profile = -> Sketch065
  Type = 0
FEATURE [PartDesign::Body] Body007  label="side_frame003"
  Group = -> [Sketch056,Pad020,Sketch058,Pad023,Sketch059,Pocket039,Sketch060,Pocket035,Sketch061,Pocket036,Sketch062,Pocket037,Sketch057,Pad021,Sketch063,Pad022,Sketch055,Pocket038,Sketch066,Pocket042,Sketch064,Pocket040,Sketch065,Pocket041]
  Origin = -> Origin007
  Placement = pos=(0,0,0) rot=(0,0,-1;1.5708rad)
  Tip = -> Pocket041
FEATURE [Sketcher::SketchObject] Sketch067
  FullyConstrained = true
  MapMode = 5
  Support = -> [XY_Plane008]
  sketch-geometry (14):
    g0: LineSegment StartX=-55 StartY=15 StartZ=0 EndX=-35 EndY=15 EndZ=0
    g1: LineSegment StartX=-35 StartY=15 StartZ=0 EndX=-35 EndY=-10 EndZ=0
    g2: LineSegment StartX=-35 StartY=-10 StartZ=0 EndX=-55 EndY=-10 EndZ=0
    g3: LineSegment StartX=-55 StartY=-10 StartZ=0 EndX=-55 EndY=15 EndZ=0
    g4: Circle CenterX=-52.5 CenterY=5 CenterZ=0 NormalX=0 NormalY=0 NormalZ=1 AngleXU=0 Radius=1.5
    g5: Circle CenterX=-37.5 CenterY=5 CenterZ=0 NormalX=0 NormalY=0 NormalZ=1 AngleXU=0 Radius=1.5
    g6: Circle CenterX=-37.5 CenterY=-5 CenterZ=0 NormalX=0 NormalY=0 NormalZ=1 AngleXU=0 Radius=1.5
    g7: Circle CenterX=-52.5 CenterY=-5 CenterZ=0 NormalX=0 NormalY=0 NormalZ=1 AngleXU=0 Radius=1.5
    g8: LineSegment StartX=-52.5 StartY=5 StartZ=0 EndX=-37.5 EndY=5 EndZ=0
    g9: LineSegment StartX=-37.5 StartY=5 StartZ=0 EndX=-37.5 EndY=-5 EndZ=0
    g10: LineSegment StartX=-37.5 StartY=-5 StartZ=0 EndX=-52.5 EndY=-5 EndZ=0
    g11: LineSegment StartX=-52.5 StartY=-5 StartZ=0 EndX=-52.5 EndY=5 EndZ=0
    g12: LineSegment StartX=-52.5 StartY=-5 StartZ=0 EndX=-55 EndY=-10 EndZ=0
    g13: LineSegment StartX=-37.5 StartY=-5 StartZ=0 EndX=-35 EndY=-10 EndZ=0
  constraints (36):
    c: Coincident(g0,g1)
    c: Coincident(g1,g2)
    c: Coincident(g2,g3)
    c: Coincident(g3,g0)
    c: Horizontal(g0)
    c: Horizontal(g2)
    c: Vertical(g1)
    c: DistanceY(g3,g3) = 25
    c: DistanceX(g0,g0) = 20
    c: DistanceX(g0,g-1) = 35
    c: Equal(g4,g5)
    c: Equal(g5,g6)
    c: Equal(g6,g7)
    c: Radius(g4) = 1.5
    c: Coincident(g8,g4)
    c: Coincident(g8,g5)
    c: Horizontal(g8)
    c: Coincident(g9,g5)
    c: Coincident(g9,g6)
    c: Vertical(g9)
    c: Coincident(g10,g6)
    c: Coincident(g10,g7)
    c: Horizontal(g10)
    c: Coincident(g11,g7)
    c: Coincident(g11,g4)
    c: Vertical(g11)
    c: DistanceX(g8,g8) = 15
    c: DistanceY(g11,g11) = 10
    c: Coincident(g12,g7)
    c: Coincident(g12,g2)
    c: Coincident(g13,g6)
    c: Coincident(g13,g1)
    c: Equal(g13,g12)
    c: Vertical(g3)
    c: DistanceY(g5,g0) = 10
    c: DistanceY(g1,g-1) = 10
FEATURE [Mesh::Feature] carriage  label="y_carriage_0"
  Placement = pos=(-165,-121.5,98) rot=(0,0,1;0rad)
FEATURE [Mesh::Feature] carriage001  label="y_carriage_1"
  Placement = pos=(-75,-121.5,98) rot=(0,0,1;0rad)
FEATURE [PartDesign::Pad] Pad024
  Direction = (1,1,1)
  Length = 3
  Length2 = 100
  Profile = -> Sketch067
  Type = 0
FEATURE [Sketcher::SketchObject] Sketch068
  ExternalGeometry = -> [Pad024]
  FullyConstrained = true
  MapMode = 5
  Placement = pos=(0,0,3) rot=(0,0,1;0rad)
  Support = -> [Pad024]
  sketch-geometry (4):
    g0: Circle CenterX=-52.5 CenterY=5 CenterZ=0 NormalX=0 NormalY=0 NormalZ=1 AngleXU=0 Radius=3
    g1: Circle CenterX=-37.5 CenterY=5 CenterZ=0 NormalX=0 NormalY=0 NormalZ=1 AngleXU=0 Radius=3
    g2: Circle CenterX=-37.5 CenterY=-5 CenterZ=0 NormalX=0 NormalY=0 NormalZ=1 AngleXU=0 Radius=3
    g3: Circle CenterX=-52.5 CenterY=-5 CenterZ=0 NormalX=0 NormalY=0 NormalZ=1 AngleXU=0 Radius=3
  constraints (8):
    c: Coincident(g0,g-3)
    c: Coincident(g1,g-4)
    c: Coincident(g2,g-5)
    c: Coincident(g3,g-6)
    c: Equal(g0,g1)
    c: Equal(g1,g3)
    c: Equal(g3,g2)
    c: Radius(g0) = 3
FEATURE [PartDesign::Pocket] Pocket043
  BaseFeature = -> Pad024
  Length = 2
  Length2 = 100
  Profile = -> Sketch068
  Type = 0
FEATURE [Sketcher::SketchObject] Sketch069
  ExternalGeometry = -> [Pocket043]
  FullyConstrained = true
  MapMode = 5
  Placement = pos=(0,0,3) rot=(0,0,1;0rad)
  Support = -> [Pocket043]
  sketch-geometry (4):
    g0: LineSegment StartX=-55 StartY=15 StartZ=0 EndX=-35 EndY=15 EndZ=0
    g1: LineSegment StartX=-35 StartY=15 StartZ=0 EndX=-35 EndY=11 EndZ=0
    g2: LineSegment StartX=-35 StartY=11 StartZ=0 EndX=-55 EndY=11 EndZ=0
    g3: LineSegment StartX=-55 StartY=11 StartZ=0 EndX=-55 EndY=15 EndZ=0
  constraints (11):
    c: Coincident(g0,g1)
    c: Coincident(g1,g2)
    c: Coincident(g2,g3)
    c: Coincident(g3,g0)
    c: Horizontal(g0)
    c: Horizontal(g2)
    c: Vertical(g1)
    c: Vertical(g3)
    c: Coincident(g0,g-3)
    c: PointOnObject(g1,g-4)
    c: DistanceY(g3,g3) = 4
FEATURE [PartDesign::Pad] Pad025
  BaseFeature = -> Pocket043
  Direction = (1,1,1)
  Length = 15
  Length2 = 100
  Profile = -> Sketch069
  Type = 0
FEATURE [Mesh::Feature] _00mm_rail_flat_x  label="x_rail"
  Placement = pos=(-306,-227.8,123) rot=(0,0,1;0rad)
FEATURE [Mesh::Feature] Mk8_Hotend
  Placement = pos=(-10,0,90) rot=(1,0,0;1.5708rad)
FEATURE [Sketcher::SketchObject] Sketch070
  ExternalGeometry = -> [Mirrored]
  FullyConstrained = true
  MapMode = 5
  Placement = pos=(0,-50,0) rot=(1,0,0;1.5708rad)
  Support = -> [Mirrored]
  sketch-geometry (1):
    g0: Circle CenterX=-43 CenterY=5 CenterZ=0 NormalX=0 NormalY=0 NormalZ=1 AngleXU=0 Radius=2.25
  constraints (3):
    c: Radius(g0) = 2.25
    c: DistanceX(g-4,g0) = 7
    c: DistanceY(g0,g-4) = 5
FEATURE [PartDesign::Pocket] Pocket044
  BaseFeature = -> Mirrored
  Length = 6
  Length2 = 100
  Profile = -> Sketch070
  Type = 0
FEATURE [PartDesign::PolarPattern] PolarPattern
  Angle = 360
  Axis = -> Z_Axis
  BaseFeature = -> Pocket044
  Occurrences = 4
  Originals = -> [Pocket044]
FEATURE [Sketcher::SketchObject] Sketch071
  ExternalGeometry = -> [PolarPattern]
  FullyConstrained = true
  MapMode = 5
  Placement = pos=(-50,0,0) rot=(0.57735,-0.57735,-0.57735;2.0944rad)
  Support = -> [PolarPattern]
  sketch-geometry (1):
    g0: Circle CenterX=43 CenterY=5 CenterZ=0 NormalX=0 NormalY=0 NormalZ=1 AngleXU=0 Radius=2.25
  constraints (3):
    c: Radius(g0) = 2.25
    c: DistanceX(g0,g-4) = 7
    c: DistanceY(g0,g-4) = 5
FEATURE [PartDesign::Pocket] Pocket045
  BaseFeature = -> PolarPattern
  Length = 6
  Length2 = 100
  Profile = -> Sketch071
  Type = 0
FEATURE [PartDesign::PolarPattern] PolarPattern001
  Angle = 360
  Axis = -> Z_Axis
  BaseFeature = -> Pocket045
  Occurrences = 4
  Originals = -> [Pocket045]
FEATURE [Sketcher::SketchObject] Sketch072
  FullyConstrained = true
  MapMode = 5
  Placement = pos=(0,50,0) rot=(0,0.707107,0.707107;3.14159rad)
  Support = -> [PolarPattern001]
  sketch-geometry (1):
    g0: Circle CenterX=-15 CenterY=5 CenterZ=0 NormalX=0 NormalY=0 NormalZ=1 AngleXU=0 Radius=2.25
  constraints (3):
    c: DistanceX(g0,g-1) = 15
    c: DistanceY(g-1,g0) = 5
    c: Radius(g0) = 2.25
FEATURE [PartDesign::Pocket] Pocket046
  BaseFeature = -> PolarPattern001
  Length = 6
  Length2 = 100
  Profile = -> Sketch072
  Type = 0
FEATURE [PartDesign::Mirrored] Mirrored001
  BaseFeature = -> Pocket046
  MirrorPlane = -> Sketch072 [V_Axis]
  Originals = -> [Pocket046]
FEATURE [Mesh::Feature] _8BYJ_48_Motor  label="z_motor"
  Placement = pos=(0,35,-29) rot=(0,0,1;3.14159rad)
FEATURE [Sketcher::SketchObject] Sketch073
  FullyConstrained = true
  MapMode = 5
  Support = -> [XY_Plane009]
  sketch-geometry (1):
    g0: Circle CenterX=0 CenterY=27 CenterZ=0 NormalX=0 NormalY=0 NormalZ=1 AngleXU=0 Radius=2.5
  constraints (3):
    c: PointOnObject(g0,g-2)
    c: Radius(g0) = 2.5
    c: DistanceY(g-1,g0) = 27
FEATURE [PartDesign::Pad] Pad026
  Direction = (1,1,1)
  Length = 80
  Length2 = 100
  Profile = -> Sketch073
  Type = 0
FEATURE [PartDesign::Body] Body009  label="threaded_rod"
  Group = -> [Sketch073,Pad026]
  Origin = -> Origin009
  Tip = -> Pad026
FEATURE [Sketcher::SketchObject] Sketch074
  FullyConstrained = true
  MapMode = 5
  Support = -> [XY_Plane010]
  sketch-geometry (5):
    g0: LineSegment StartX=-37.5 StartY=35 StartZ=0 EndX=37.5 EndY=35 EndZ=0
    g1: LineSegment StartX=37.5 StartY=35 StartZ=0 EndX=37.5 EndY=-37 EndZ=0
    g2: LineSegment StartX=37.5 StartY=-37 StartZ=0 EndX=-37.5 EndY=-37 EndZ=0
    g3: LineSegment StartX=-37.5 StartY=-37 StartZ=0 EndX=-37.5 EndY=35 EndZ=0
    g4: Circle CenterX=0 CenterY=27 CenterZ=0 NormalX=0 NormalY=0 NormalZ=1 AngleXU=0 Radius=5
  constraints (14):
    c: Coincident(g0,g1)
    c: Coincident(g1,g2)
    c: Coincident(g2,g3)
    c: Coincident(g3,g0)
    c: Horizontal(g2)
    c: Vertical(g1)
    c: Symmetric(g0,g0,g-2)
    c: DistanceY(g1,g1) = 72
    c: DistanceX(g0,g0) = 75
    c: Vertical(g3)
    c: DistanceY(g-1,g0) = 35
    c: PointOnObject(g4,g-2)
    c: DistanceY(g-1,g4) = 27
    c: Radius(g4) = 5
FEATURE [PartDesign::Pad] Pad027
  Direction = (1,1,1)
  Length = 5
  Length2 = 100
  Profile = -> Sketch074
  Type = 0
FEATURE [Sketcher::SketchObject] Sketch076
  FullyConstrained = true
  MapMode = 5
  Placement = pos=(0,0,0) rot=(1,0,0;3.14159rad)
  sketch-geometry (4):
    g0: LineSegment StartX=-7.5 StartY=-19.5 StartZ=0 EndX=7.5 EndY=-19.5 EndZ=0
    g1: LineSegment StartX=7.5 StartY=-19.5 StartZ=0 EndX=7.5 EndY=-34.5 EndZ=0
    g2: LineSegment StartX=7.5 StartY=-34.5 StartZ=0 EndX=-7.5 EndY=-34.5 EndZ=0
    g3: LineSegment StartX=-7.5 StartY=-34.5 StartZ=0 EndX=-7.5 EndY=-19.5 EndZ=0
  constraints (11):
    c: Coincident(g0,g1)
    c: Coincident(g1,g2)
    c: Coincident(g2,g3)
    c: Coincident(g3,g0)
    c: Horizontal(g2)
    c: Vertical(g1)
    c: Vertical(g3)
    c: Symmetric(g0,g0,g-2)
    c: DistanceX(g0,g0) = 15
    c: DistanceY(g3,g3) = 15
    c: DistanceY(g0,g-1) = 19.5
FEATURE [PartDesign::Pad] Pad029
  BaseFeature = -> Pad027
  Direction = (1,1,1)
  Length = 6
  Length2 = 100
  Profile = -> Sketch076
  Type = 0
FEATURE [Sketcher::SketchObject] Sketch077
  ExternalGeometry = -> [Pad029]
  FullyConstrained = true
  MapMode = 5
  Placement = pos=(0,34.5,0) rot=(0,0.707107,0.707107;3.14159rad)
  Support = -> [Pad029]
  sketch-geometry (4):
    g0: LineSegment StartX=-3.9 StartY=-1 StartZ=0 EndX=3.9 EndY=-1 EndZ=0
    g1: LineSegment StartX=3.9 StartY=-1 StartZ=0 EndX=3.9 EndY=-5 EndZ=0
    g2: LineSegment StartX=3.9 StartY=-5 StartZ=0 EndX=-3.9 EndY=-5 EndZ=0
    g3: LineSegment StartX=-3.9 StartY=-5 StartZ=0 EndX=-3.9 EndY=-1 EndZ=0
  constraints (11):
    c: Coincident(g0,g1)
    c: Coincident(g1,g2)
    c: Coincident(g2,g3)
    c: Coincident(g3,g0)
    c: Horizontal(g2)
    c: Vertical(g1)
    c: Vertical(g3)
    c: Symmetric(g0,g0,g-2)
    c: DistanceX(g2,g2) = 7.8
    c: DistanceY(g1,g1) = 4
    c: DistanceY(g0,g-4) = 6
FEATURE [PartDesign::Pocket] Pocket047
  BaseFeature = -> Pad029
  Length = 15
  Length2 = 100
  Profile = -> Sketch077
  Type = 0
FEATURE [Mesh::Feature] carriage_z  label="carriage_z_0"
  Placement = pos=(-250.5,-198,-10) rot=(0,0,1;0rad)
FEATURE [Mesh::Feature] carriage_z001  label="carriage_z_1"
  Placement = pos=(-220.5,-198,-10) rot=(0,0,1;0rad)
FEATURE [Sketcher::SketchObject] Sketch081
  FullyConstrained = true
  MapMode = 5
  Support = -> [XY_Plane011]
  sketch-geometry (8):
    g0: LineSegment StartX=-50 StartY=50 StartZ=0 EndX=50 EndY=50 EndZ=0
    g1: LineSegment StartX=50 StartY=50 StartZ=0 EndX=50 EndY=-50 EndZ=0
    g2: LineSegment StartX=50 StartY=-50 StartZ=0 EndX=-50 EndY=-50 EndZ=0
    g3: LineSegment StartX=-50 StartY=-50 StartZ=0 EndX=-50 EndY=50 EndZ=0
    g4: LineSegment StartX=-40 StartY=40 StartZ=0 EndX=40 EndY=40 EndZ=0
    g5: LineSegment StartX=40 StartY=40 StartZ=0 EndX=40 EndY=-40 EndZ=0
    g6: LineSegment StartX=40 StartY=-40 StartZ=0 EndX=-40 EndY=-40 EndZ=0
    g7: LineSegment StartX=-40 StartY=-40 StartZ=0 EndX=-40 EndY=40 EndZ=0
  constraints (20):
    c: Coincident(g0,g1)
    c: Coincident(g1,g2)
    c: Coincident(g2,g3)
    c: Coincident(g3,g0)
    c: Horizontal(g2)
    c: Vertical(g1)
    c: Coincident(g4,g5)
    c: Coincident(g5,g6)
    c: Coincident(g6,g7)
    c: Coincident(g7,g4)
    c: Horizontal(g6)
    c: Vertical(g5)
    c: Symmetric(g4,g4,g-2)
    c: Symmetric(g4,g6,g-1)
    c: Equal(g7,g4)
    c: Equal(g0,g3)
    c: Symmetric(g0,g2,g-1)
    c: Symmetric(g0,g0,g-2)
    c: DistanceY(g4,g0) = 10
    c: DistanceY(g3,g3) = 100
FEATURE [PartDesign::Pad] Pad032
  Direction = (1,1,1)
  Length = 10
  Length2 = 100
  Profile = -> Sketch081
  Type = 0
FEATURE [Sketcher::SketchObject] Sketch083
  FullyConstrained = false
  MapMode = 5
  Placement = pos=(0,-50,0) rot=(1,0,0;1.5708rad)
  sketch-geometry (1):
    g0: Circle CenterX=-43 CenterY=5 CenterZ=0 NormalX=0 NormalY=0 NormalZ=1 AngleXU=0 Radius=2.25
  constraints (1):
    c: Radius(g0) = 2.25
FEATURE [PartDesign::Pocket] Pocket051
  BaseFeature = -> Pad032
  Length = 6
  Length2 = 100
  Profile = -> Sketch083
  Type = 0
FEATURE [PartDesign::PolarPattern] PolarPattern002
  Angle = 360
  Axis = -> Z_Axis011
  BaseFeature = -> Pocket051
  Occurrences = 4
  Originals = -> [Pocket051]
FEATURE [Sketcher::SketchObject] Sketch082
  ExternalGeometry = -> [PolarPattern002]
  FullyConstrained = true
  MapMode = 5
  Placement = pos=(-50,0,0) rot=(0.57735,-0.57735,-0.57735;2.0944rad)
  Support = -> [PolarPattern002]
  sketch-geometry (1):
    g0: Circle CenterX=43 CenterY=5 CenterZ=0 NormalX=0 NormalY=0 NormalZ=1 AngleXU=0 Radius=2.25
  constraints (3):
    c: Radius(g0) = 2.25
    c: DistanceX(g0,g-4) = 7
    c: DistanceY(g0,g-4) = 5
FEATURE [PartDesign::Pocket] Pocket050
  BaseFeature = -> PolarPattern002
  Length = 6
  Length2 = 100
  Profile = -> Sketch082
  Type = 0
FEATURE [PartDesign::PolarPattern] PolarPattern003
  Angle = 360
  Axis = -> Z_Axis011
  BaseFeature = -> Pocket050
  Occurrences = 4
  Originals = -> [Pocket050]
FEATURE [Sketcher::SketchObject] Sketch084
  FullyConstrained = true
  MapMode = 5
  Placement = pos=(0,50,0) rot=(0,0.707107,0.707107;3.14159rad)
  Support = -> [PolarPattern003]
  sketch-geometry (1):
    g0: Circle CenterX=-15 CenterY=5 CenterZ=0 NormalX=0 NormalY=0 NormalZ=1 AngleXU=0 Radius=2.25
  constraints (3):
    c: DistanceX(g0,g-1) = 15
    c: DistanceY(g-1,g0) = 5
    c: Radius(g0) = 2.25
FEATURE [PartDesign::Pocket] Pocket049
  BaseFeature = -> PolarPattern003
  Length = 6
  Length2 = 100
  Profile = -> Sketch084
  Type = 0
FEATURE [PartDesign::Mirrored] Mirrored003
  BaseFeature = -> Pocket049
  MirrorPlane = -> Sketch084 [V_Axis]
  Originals = -> [Pocket049]
FEATURE [Sketcher::SketchObject] Sketch085
  ExternalGeometry = -> [Pad025]
  FullyConstrained = true
  MapMode = 5
  Placement = pos=(0,11,0) rot=(1,0,0;1.5708rad)
  Support = -> [Pad025]
  sketch-geometry (9):
    g0: Circle CenterX=-40 CenterY=13 CenterZ=0 NormalX=0 NormalY=0 NormalZ=1 AngleXU=0 Radius=1.65
    g1: LineSegment StartX=-53 StartY=12 StartZ=0 EndX=-51 EndY=12 EndZ=0
    g2: LineSegment StartX=-51 StartY=12 StartZ=0 EndX=-51 EndY=5 EndZ=0
    g3: LineSegment StartX=-51 StartY=5 StartZ=0 EndX=-53 EndY=5 EndZ=0
    g4: LineSegment StartX=-53 StartY=5 StartZ=0 EndX=-53 EndY=12 EndZ=0
    g5: LineSegment StartX=-45 StartY=12 StartZ=0 EndX=-47 EndY=12 EndZ=0
    g6: LineSegment StartX=-47 StartY=12 StartZ=0 EndX=-47 EndY=5 EndZ=0
    g7: LineSegment StartX=-47 StartY=5 StartZ=0 EndX=-45 EndY=5 EndZ=0
    g8: LineSegment StartX=-45 StartY=5 StartZ=0 EndX=-45 EndY=12 EndZ=0
  constraints (27):
    c: Radius(g0) = 1.65
    c: DistanceY(g0,g-6) = 5
    c: DistanceX(g0,g-6) = 5
    c: Coincident(g1,g2)
    c: Coincident(g2,g3)
    c: Coincident(g3,g4)
    c: Coincident(g4,g1)
    c: Horizontal(g1)
    c: Horizontal(g3)
    c: Vertical(g2)
    c: Vertical(g4)
    c: Coincident(g5,g6)
    c: Coincident(g6,g7)
    c: Coincident(g7,g8)
    c: Coincident(g8,g5)
    c: Horizontal(g5)
    c: Horizontal(g7)
    c: Vertical(g6)
    c: Vertical(g8)
    c: DistanceY(g5,g1) = 0
    c: Equal(g1,g5)
    c: Equal(g2,g8)
    c: DistanceY(g4,g4) = 7
    c: DistanceX(g1,g1) = 2
    c: DistanceX(g-4,g3) = 2
    c: DistanceY(g-4,g3) = 2
    c: DistanceX(g2,g7) = 6
FEATURE [PartDesign::Pocket] Pocket052
  BaseFeature = -> Pad025
  Length = 5
  Length2 = 100
  Profile = -> Sketch085
  Type = 0
FEATURE [PartDesign::Body] Body008  label="y_carriage"
  Group = -> [Sketch067,Pad024,Sketch068,Pocket043,Sketch069,Pad025,Sketch085,Pocket052]
  Origin = -> Origin008
  Placement = pos=(0,0,121) rot=(0,0,1;0rad)
  Tip = -> Pocket052
FEATURE [Sketcher::SketchObject] Sketch086
  ExternalGeometry = -> [Pocket047]
  FullyConstrained = true
  MapMode = 5
  Placement = pos=(0,0,0) rot=(1,0,0;3.14159rad)
  Support = -> [Pocket047]
  sketch-geometry (8):
    g0: LineSegment StartX=-7.5 StartY=-31 StartZ=0 EndX=-25.5 EndY=-31 EndZ=0
    g1: LineSegment StartX=-25.5 StartY=-31 StartZ=0 EndX=-25.5 EndY=-35 EndZ=0
    g2: LineSegment StartX=-25.5 StartY=-35 StartZ=0 EndX=-7.5 EndY=-35 EndZ=0
    g3: LineSegment StartX=-7.5 StartY=-35 StartZ=0 EndX=-7.5 EndY=-31 EndZ=0
    g4: LineSegment StartX=7.5 StartY=-31 StartZ=0 EndX=25.5 EndY=-31 EndZ=0
    g5: LineSegment StartX=25.5 StartY=-31 StartZ=0 EndX=25.5 EndY=-35 EndZ=0
    g6: LineSegment StartX=25.5 StartY=-35 StartZ=0 EndX=7.5 EndY=-35 EndZ=0
    g7: LineSegment StartX=7.5 StartY=-35 StartZ=0 EndX=7.5 EndY=-31 EndZ=0
  constraints (24):
    c: PointOnObject(g0,g-3)
    c: Horizontal(g0)
    c: Coincident(g0,g1)
    c: PointOnObject(g1,g-4)
    c: Vertical(g1)
    c: Coincident(g1,g2)
    c: PointOnObject(g2,g-4)
    c: Coincident(g2,g3)
    c: Coincident(g3,g0)
    c: Vertical(g3)
    c: DistanceX(g0,g0) = 18
    c: DistanceY(g1,g1) = 4
    c: Coincident(g4,g5)
    c: Coincident(g5,g6)
    c: Coincident(g6,g7)
    c: Coincident(g7,g4)
    c: Horizontal(g4)
    c: Horizontal(g6)
    c: Vertical(g5)
    c: Vertical(g7)
    c: PointOnObject(g4,g-5)
    c: PointOnObject(g5,g-4)
    c: DistanceX(g4,g4) = 18
    c: DistanceY(g5,g5) = 4
FEATURE [PartDesign::Pad] Pad033
  BaseFeature = -> Pocket047
  Direction = (1,1,1)
  Length = 20
  Length2 = 100
  Profile = -> Sketch086
  Type = 0
FEATURE [Sketcher::SketchObject] Sketch087
  ExternalGeometry = -> [Pad033]
  FullyConstrained = true
  MapMode = 5
  Placement = pos=(0,31,0) rot=(1,0,0;1.5708rad)
  Support = -> [Pad033]
  sketch-geometry (2):
    g0: Circle CenterX=-22.7 CenterY=-2 CenterZ=0 NormalX=0 NormalY=0 NormalZ=1 AngleXU=0 Radius=1.5
    g1: Circle CenterX=-22.7 CenterY=-12 CenterZ=0 NormalX=0 NormalY=0 NormalZ=1 AngleXU=0 Radius=1.5
  constraints (6):
    c: Equal(g0,g1)
    c: Radius(g0) = 1.5
    c: DistanceX(g-3,g0) = 2.8
    c: DistanceY(g0,g-3) = 2
    c: DistanceY(g1,g0) = 10
    c: DistanceX(g0,g1) = 0
FEATURE [PartDesign::Pocket] Pocket053
  BaseFeature = -> Pad033
  Length = 5
  Length2 = 100
  Profile = -> Sketch087
  Type = 0
FEATURE [Sketcher::SketchObject] Sketch088
  ExternalGeometry = -> [Pocket053]
  FullyConstrained = true
  MapMode = 5
  Placement = pos=(0,31,0) rot=(1,0,0;1.5708rad)
  Support = -> [Pocket053]
  sketch-geometry (2):
    g0: Circle CenterX=-22.7 CenterY=-2 CenterZ=0 NormalX=0 NormalY=0 NormalZ=1 AngleXU=0 Radius=3
    g1: Circle CenterX=-22.7 CenterY=-12 CenterZ=0 NormalX=0 NormalY=0 NormalZ=1 AngleXU=0 Radius=3
  constraints (4):
    c: Coincident(g0,g-3)
    c: Radius(g0) = 3
    c: Coincident(g1,g-4)
    c: Radius(g1) = 3
FEATURE [PartDesign::Pocket] Pocket054
  BaseFeature = -> Pocket053
  Length = 2
  Length2 = 100
  Profile = -> Sketch088
  Type = 0
FEATURE [PartDesign::Mirrored] Mirrored004
  BaseFeature = -> Pocket054
  MirrorPlane = -> Sketch087 [V_Axis]
  Originals = -> [Pocket053,Pocket054]
FEATURE [PartDesign::Body] Body010  label="bed"
  Group = -> [Sketch074,Pad027,Sketch076,Pad029,Sketch077,Pocket047,Sketch086,Pad033,Sketch087,Pocket053,Sketch088,Pocket054,Mirrored004]
  Origin = -> Origin010
  Placement = pos=(0,0,30) rot=(0,0,1;0rad)
  Tip = -> Mirrored004
FEATURE [Sketcher::SketchObject] Sketch089
  FullyConstrained = true
  MapMode = 5
  Placement = pos=(0,0,0) rot=(1,0,0;1.5708rad)
  Support = -> [XZ_Plane012]
  sketch-geometry (6):
    g0: LineSegment StartX=-45 StartY=38.5 StartZ=0 EndX=45 EndY=38.5 EndZ=0
    g1: LineSegment StartX=45 StartY=38.5 StartZ=0 EndX=45 EndY=29.5 EndZ=0
    g2: LineSegment StartX=45 StartY=29.5 StartZ=0 EndX=-45 EndY=29.5 EndZ=0
    g3: LineSegment StartX=-45 StartY=29.5 StartZ=0 EndX=-45 EndY=38.5 EndZ=0
    g4: Circle CenterX=-40 CenterY=34 CenterZ=0 NormalX=0 NormalY=0 NormalZ=1 AngleXU=0 Radius=1.6
    g5: Circle CenterX=40 CenterY=34 CenterZ=0 NormalX=0 NormalY=0 NormalZ=1 AngleXU=0 Radius=1.6
  constraints (18):
    c: Coincident(g0,g1)
    c: Coincident(g1,g2)
    c: Coincident(g2,g3)
    c: Coincident(g3,g0)
    c: Horizontal(g0)
    c: Horizontal(g2)
    c: Vertical(g1)
    c: Vertical(g3)
    c: DistanceX(g0,g0) = 90
    c: DistanceY(g3,g3) = 9
    c: DistanceY(g-1,g2) = 29.5
    c: DistanceX(g2,g-1) = 45
    c: DistanceX(g0,g4) = 5
    c: DistanceY(g4,g0) = 4.5
    c: Radius(g4) = 1.6
    c: Radius(g5) = 1.6
    c: DistanceY(g5,g0) = 4.5
    c: DistanceX(g5,g0) = 5
FEATURE [PartDesign::Pad] Pad034
  Direction = (1,1,1)
  Length = 4
  Length2 = 100
  Placement = pos=(0,0,0) rot=(1,0,0;1.5708rad)
  Profile = -> Sketch089
  Type = 0
FEATURE [Sketcher::SketchObject] Sketch090
  ExternalGeometry = -> [Pad034]
  FullyConstrained = true
  MapMode = 5
  Placement = pos=(0,1e-16,0) rot=(-1,0,0;1.5708rad)
  Support = -> [Pad034]
  sketch-geometry (7):
    g0: LineSegment StartX=-37 StartY=-32.2679 StartZ=0 EndX=-40 EndY=-30.5359 EndZ=0
    g1: LineSegment StartX=-40 StartY=-30.5359 StartZ=0 EndX=-43 EndY=-32.2679 EndZ=0
    g2: LineSegment StartX=-43 StartY=-32.2679 StartZ=0 EndX=-43 EndY=-35.7321 EndZ=0
    g3: LineSegment StartX=-43 StartY=-35.7321 StartZ=0 EndX=-40 EndY=-37.4641 EndZ=0
    g4: LineSegment StartX=-40 StartY=-37.4641 StartZ=0 EndX=-37 EndY=-35.7321 EndZ=0
    g5: LineSegment StartX=-37 StartY=-35.7321 StartZ=0 EndX=-37 EndY=-32.2679 EndZ=0
    g6: Circle CenterX=-40 CenterY=-34 CenterZ=0 NormalX=0 NormalY=0 NormalZ=1 AngleXU=0 Radius=3.4641
  constraints (16):
    c: Coincident(g0,g1)
    c: Coincident(g1,g2)
    c: Coincident(g2,g3)
    c: Coincident(g3,g4)
    c: Coincident(g4,g5)
    c: Coincident(g5,g0)
    c: Equal(g0, g1-g5) x5
    c: PointOnObject(g0,g6)
    c: PointOnObject(g1,g6)
    c: PointOnObject(g2,g6)
    c: PointOnObject(g3,g6)
    c: PointOnObject(g4,g6)
    c: PointOnObject(g5,g6)
    c: Coincident(g6,g-3)
    c: Vertical(g5)
    c: DistanceX(g1,g0) = 6
FEATURE [PartDesign::Pocket] Pocket055
  BaseFeature = -> Pad034
  Length = 3
  Length2 = 100
  Placement = pos=(0,0,0) rot=(1,0,0;1.5708rad)
  Profile = -> Sketch090
  Type = 0
FEATURE [PartDesign::Mirrored] Mirrored005
  BaseFeature = -> Pocket055
  MirrorPlane = -> Sketch090 [V_Axis]
  Originals = -> [Pocket055]
  Placement = pos=(0,0,0) rot=(1,0,0;1.5708rad)
FEATURE [PartDesign::Body] Body012  label="x_brace"
  Group = -> [Sketch089,Pad034,Sketch090,Pocket055,Mirrored005]
  Origin = -> Origin012
  Placement = pos=(0,19,100) rot=(0,0,1;0rad)
  Tip = -> Mirrored005
FEATURE [Mesh::Feature] carriage_z002  label="carriage_z_002"
  Placement = pos=(-33,-232,370) rot=(0,1,0;1.5708rad)
FEATURE [Mesh::Feature] _8BYJ_48_Motor001  label="y_motor"
  Placement = pos=(-52,71,95) rot=(0,0,1;3.14159rad)
FEATURE [Mesh::Feature] GT2_20T_Pulley
  Placement = pos=(-52,63,118) rot=(0,0,1;0rad)
FEATURE [Sketcher::SketchObject] Sketch091
  FullyConstrained = false
  MapMode = 5
  Support = -> [XY_Plane013]
  sketch-geometry (24):
    g0: LineSegment StartX=-53 StartY=-7 StartZ=0 EndX=-35 EndY=-7 EndZ=0
    g1: LineSegment StartX=-35 StartY=-7 StartZ=0 EndX=-35 EndY=0 EndZ=0
    g2: LineSegment StartX=-35 StartY=0 StartZ=0 EndX=-27.9146 EndY=0 EndZ=0
    g3: LineSegment StartX=-27.9146 StartY=0 StartZ=0 EndX=-27.9146 EndY=25 EndZ=0
    g4: LineSegment StartX=-27.9146 StartY=25 StartZ=0 EndX=-44 EndY=25 EndZ=0
    g5: LineSegment StartX=-76.0854 StartY=25 StartZ=0 EndX=-76.0854 EndY=0 EndZ=0
    g6: LineSegment StartX=-76.0854 StartY=0 StartZ=0 EndX=-65.3848 EndY=0 EndZ=0
    g7: LineSegment StartX=-65.3848 StartY=0 StartZ=0 EndX=-58 EndY=-7.38476 EndZ=0
    g8: LineSegment StartX=-58 StartY=-7.38476 StartZ=0 EndX=-58 EndY=-25 EndZ=0
    g9: LineSegment StartX=-58 StartY=-25 StartZ=0 EndX=-53 EndY=-25 EndZ=0
    g10: LineSegment StartX=-53 StartY=-25 StartZ=0 EndX=-53 EndY=-7 EndZ=0
    g11: LineSegment StartX=-52 StartY=0 StartZ=0 EndX=-52 EndY=30 EndZ=0
    g12: ArcOfCircle CenterX=-69.5 CenterY=11 CenterZ=0 NormalX=0 NormalY=0 NormalZ=1 AngleXU=0 Radius=2.1 StartAngle=3.14159 EndAngle=6.28319
    g13: ArcOfCircle CenterX=-69.5 CenterY=18 CenterZ=0 NormalX=0 NormalY=0 NormalZ=1 AngleXU=0 Radius=2.1 StartAngle=5e-16 EndAngle=3.14159
    g14: LineSegment StartX=-67.4 StartY=11 StartZ=0 EndX=-67.4 EndY=18 EndZ=0
    g15: LineSegment StartX=-71.6 StartY=11 StartZ=0 EndX=-71.6 EndY=18 EndZ=0
    g16: ArcOfCircle CenterX=-34.5 CenterY=11 CenterZ=0 NormalX=0 NormalY=0 NormalZ=1 AngleXU=0 Radius=2.1 StartAngle=3.14159 EndAngle=6.28319
    g17: ArcOfCircle CenterX=-34.5 CenterY=18 CenterZ=0 NormalX=0 NormalY=0 NormalZ=1 AngleXU=0 Radius=2.1 StartAngle=0 EndAngle=3.14159
    g18: LineSegment StartX=-32.4 StartY=11 StartZ=0 EndX=-32.4 EndY=18 EndZ=0
    g19: LineSegment StartX=-36.6 StartY=11 StartZ=0 EndX=-36.6 EndY=18 EndZ=0
    g20: ArcOfCircle CenterX=-52 CenterY=11.0226 CenterZ=0 NormalX=0 NormalY=0 NormalZ=1 AngleXU=0 Radius=14.5 StartAngle=2.15523 EndAngle=7.26955
    g21: LineSegment StartX=-44 StartY=23.116 StartZ=0 EndX=-44 EndY=25 EndZ=0
    g22: LineSegment StartX=-60 StartY=23.116 StartZ=0 EndX=-60 EndY=25 EndZ=0
    g23: LineSegment StartX=-60 StartY=25 StartZ=0 EndX=-76.0854 EndY=25 EndZ=0
  constraints (65):
    c: Horizontal(g0)
    c: Coincident(g0,g1)
    c: PointOnObject(g1,g-1)
    c: Vertical(g1)
    c: Coincident(g1,g2)
    c: PointOnObject(g2,g-1)
    c: Coincident(g2,g3)
    c: Vertical(g3)
    c: Coincident(g3,g4)
    c: Horizontal(g4)
    c: Coincident(g23,g5)
    c: PointOnObject(g5,g-1)
    c: Vertical(g5)
    c: Coincident(g5,g6)
    c: PointOnObject(g6,g-1)
    c: Coincident(g6,g7)
    c: Coincident(g7,g8)
    c: Vertical(g8)
    c: Coincident(g8,g9)
    c: Horizontal(g9)
    c: Coincident(g9,g10)
    c: Coincident(g10,g0)
    c: Vertical(g10)
    c: Equal(g0,g10)
    c: DistanceX(g0,g0) = 18
    c: Angle(g7,g8) = 2.35619
    c: PointOnObject(g11,g-1)
    c: DistanceX(g11,g-1) = 52
    c: Symmetric(g23,g3,g11)
    c: DistanceY(g11,g11) = 30
    c: DistanceY(g5,g5) = 25
    c: Tangent(g12,g15) = 1.5708
    c: Tangent(g12,g14) = -1.5708
    c: Tangent(g14,g13) = -1.5708
    c: Tangent(g15,g13) = 1.5708
    c: Vertical(g14)
    c: Equal(g12,g13)
    c: Tangent(g16,g19) = 1.5708
    c: Tangent(g16,g18) = -1.5708
    c: Tangent(g18,g17) = -1.5708
    c: Tangent(g19,g17) = 1.5708
    c: Vertical(g18)
    c: Equal(g16,g17)
    c: DistanceX(g13,g13) = 4.2
    c: DistanceX(g17,g17) = 4.2
    c: Equal(g15,g19)
    c: DistanceY(g15,g15) = 7
    c: DistanceX(g12,g-1) = 69.5
    c: DistanceY(g-1,g12) = 11
    c: DistanceY(g17,g13) = 0
    c: DistanceX(g13,g17) = 35
    c: PointOnObject(g20,g11)
    c: Radius(g20) = 14.5
    c: Vertical(g21)
    c: Vertical(g22)
    c: Symmetric(g22,g21,g11)
    c: DistanceX(g22,g11) = 8
    c: Tangent(g4,g23)
    c: Coincident(g4,g21)
    c: PointOnObject(g23,g22)
    c: Coincident(g20,g22)
    c: Coincident(g20,g21)
    c: DistanceY(g1,g1) = 7
    c: DistanceX(g9,g9) = 5
    c: DistanceX(g0,g-1) = 53
FEATURE [PartDesign::Pad] Pad035
  Direction = (1,1,1)
  Length = 3
  Length2 = 100
  Profile = -> Sketch091
  Type = 0
FEATURE [Sketcher::SketchObject] Sketch092
  ExternalGeometry = -> [Pad035]
  FullyConstrained = false
  MapMode = 5
  Placement = pos=(0,0,0) rot=(1,0,0;3.14159rad)
  Support = -> [Pad035]
  sketch-geometry (8):
    g0: LineSegment StartX=-53 StartY=25 StartZ=0 EndX=-58 EndY=25 EndZ=0
    g1: LineSegment StartX=-58 StartY=25 StartZ=0 EndX=-58 EndY=7.38476 EndZ=0
    g2: LineSegment StartX=-58 StartY=7.38476 StartZ=0 EndX=-58 EndY=2.56476 EndZ=0
    g3: LineSegment StartX=-35 StartY=-1.8e-15 StartZ=0 EndX=-35 EndY=7 EndZ=0
    g4: LineSegment StartX=-35 StartY=7 StartZ=0 EndX=-53 EndY=7 EndZ=0
    g5: LineSegment StartX=-53 StartY=7 StartZ=0 EndX=-53 EndY=25 EndZ=0
    g6: LineSegment StartX=-41.98 StartY=-1.8e-15 StartZ=0 EndX=-35 EndY=-1.8e-15 EndZ=0
    g7: ArcOfCircle CenterX=-52.0224 CenterY=-11.4121 CenterZ=0 NormalX=0 NormalY=0 NormalZ=1 AngleXU=0 Radius=15.2015 StartAngle=0.849156 EndAngle=1.97494
  constraints (19):
    c: Coincident(g-3,g0)
    c: Coincident(g0,g-4)
    c: Coincident(g0,g1)
    c: Coincident(g1,g-4)
    c: Coincident(g1,g2)
    c: Coincident(g3,g-5)
    c: Coincident(g3,g4)
    c: Horizontal(g4)
    c: Coincident(g4,g5)
    c: Coincident(g5,g0)
    c: Vertical(g5)
    c: Coincident(g6,g3)
    c: Horizontal(g6)
    c: Vertical(g3)
    c: Vertical(g2)
    c: Coincident(g7,g6)
    c: Coincident(g7,g2)
    c: DistanceY(g2,g2) = 4.82
    c: DistanceX(g6,g6) = 6.98
FEATURE [PartDesign::Pad] Pad036
  BaseFeature = -> Pad035
  Direction = (1,1,1)
  Length = 10
  Length2 = 100
  Profile = -> Sketch092
  Type = 0
FEATURE [Sketcher::SketchObject] Sketch093
  ExternalGeometry = -> [Pad036]
  FullyConstrained = true
  MapMode = 5
  Placement = pos=(-58,0,0) rot=(0.57735,-0.57735,-0.57735;2.0944rad)
  Support = -> [Pad036]
  sketch-geometry (1):
    g0: Circle CenterX=17 CenterY=-5 CenterZ=0 NormalX=0 NormalY=0 NormalZ=1 AngleXU=0 Radius=1.6
  constraints (3):
    c: Radius(g0) = 1.6
    c: DistanceX(g0,g-4) = 8
    c: DistanceY(g0,g-4) = 5
FEATURE [PartDesign::Pocket] Pocket056
  BaseFeature = -> Pad036
  Length = 5
  Length2 = 100
  Profile = -> Sketch093
  Type = 0
FEATURE [Sketcher::SketchObject] Sketch094
  ExternalGeometry = -> [Pocket056]
  FullyConstrained = true
  MapMode = 5
  Placement = pos=(-58,0,0) rot=(0.57735,-0.57735,-0.57735;2.0944rad)
  Support = -> [Pocket056]
  sketch-geometry (1):
    g0: Circle CenterX=17 CenterY=-5 CenterZ=0 NormalX=0 NormalY=0 NormalZ=1 AngleXU=0 Radius=3.5
  constraints (2):
    c: Coincident(g0,g-3)
    c: Radius(g0) = 3.5
FEATURE [PartDesign::Pocket] Pocket057
  BaseFeature = -> Pocket056
  Length = 3.5
  Length2 = 100
  Profile = -> Sketch094
  Type = 0
FEATURE [Sketcher::SketchObject] Sketch095
  ExternalGeometry = -> [Pocket057]
  FullyConstrained = true
  MapMode = 5
  Placement = pos=(0,1.8e-15,0) rot=(0,0.707107,0.707107;3.14159rad)
  Support = -> [Pocket057]
  sketch-geometry (1):
    g0: Circle CenterX=43 CenterY=-5 CenterZ=0 NormalX=0 NormalY=0 NormalZ=1 AngleXU=0 Radius=1.6
  constraints (3):
    c: Radius(g0) = 1.6
    c: DistanceY(g0,g-3) = 5
    c: DistanceX(g-3,g0) = 8
FEATURE [PartDesign::Pocket] Pocket058
  BaseFeature = -> Pocket057
  Length = 10
  Length2 = 100
  Profile = -> Sketch095
  Type = 0
FEATURE [Sketcher::SketchObject] Sketch096
  ExternalGeometry = -> [Pocket058]
  FullyConstrained = true
  MapMode = 5
  Placement = pos=(0,1.8e-15,0) rot=(0,0.707107,0.707107;3.14159rad)
  Support = -> [Pocket058]
  sketch-geometry (1):
    g0: Circle CenterX=43 CenterY=-5 CenterZ=0 NormalX=0 NormalY=0 NormalZ=1 AngleXU=0 Radius=3.5
  constraints (2):
    c: Coincident(g0,g-3)
    c: Radius(g0) = 3.5
FEATURE [PartDesign::Pocket] Pocket059
  BaseFeature = -> Pocket058
  Length = 6
  Length2 = 100
  Profile = -> Sketch096
  Type = 0
FEATURE [PartDesign::Body] Body013  label="y_motor_mount"
  Group = -> [Sketch091,Pad035,Sketch092,Pad036,Sketch093,Pocket056,Sketch094,Pocket057,Sketch095,Pocket058,Sketch096,Pocket059]
  Origin = -> Origin013
  Placement = pos=(0,60,110) rot=(0,0,1;0rad)
  Tip = -> Pocket059
FEATURE [Sketcher::SketchObject] Sketch097
  ExternalGeometry = -> [Mirrored001]
  FullyConstrained = true
  MapMode = 5
  Placement = pos=(0,0,10) rot=(0,0,1;0rad)
  Support = -> [Mirrored001]
  sketch-geometry (4):
    g0: LineSegment StartX=-35 StartY=-50 StartZ=0 EndX=-35 EndY=-40 EndZ=0
    g1: LineSegment StartX=35 StartY=-50 StartZ=0 EndX=35 EndY=-40 EndZ=0
    g2: LineSegment StartX=-35 StartY=-40 StartZ=0 EndX=35 EndY=-40 EndZ=0
    g3: LineSegment StartX=35 StartY=-50 StartZ=0 EndX=-35 EndY=-50 EndZ=0
  constraints (12):
    c: PointOnObject(g0,g-4)
    c: PointOnObject(g0,g-3)
    c: Angle(g-4,g0) = 1.5708
    c: DistanceX(g0,g-1) = 35
    c: PointOnObject(g1,g-4)
    c: PointOnObject(g1,g-3)
    c: Angle(g1,g-4) = 1.5708
    c: DistanceX(g-1,g1) = 35
    c: Coincident(g2,g0)
    c: Coincident(g2,g1)
    c: Coincident(g3,g1)
    c: Coincident(g3,g0)
FEATURE [PartDesign::Pocket] Pocket060
  BaseFeature = -> Mirrored001
  Length = 10
  Length2 = 100
  Profile = -> Sketch097
  Type = 0
FEATURE [PartDesign::Body] Body  label="top_frame"
  Group = -> [Sketch,Pad,Sketch002,Pocket,Mirrored,Sketch070,Pocket044,PolarPattern,Sketch071,Pocket045,PolarPattern001,Sketch072,Pocket046,Mirrored001,Sketch097,Pocket060]
  Origin = -> Origin
  Placement = pos=(0,0,100) rot=(0,0,1;0rad)
  Tip = -> Pocket060
FEATURE [Sketcher::SketchObject] Sketch098
  ExternalGeometry = -> [Mirrored003]
  FullyConstrained = true
  MapMode = 5
  Placement = pos=(0,0,0) rot=(1,0,0;3.14159rad)
  Support = -> [Mirrored003]
  sketch-geometry (7):
    g0: LineSegment StartX=-23 StartY=-40 StartZ=0 EndX=-23 EndY=-33.5 EndZ=0
    g1: LineSegment StartX=-12 StartY=-40 StartZ=0 EndX=-12 EndY=-33.5 EndZ=0
    g2: Circle CenterX=-17.5 CenterY=-35 CenterZ=0 NormalX=0 NormalY=0 NormalZ=1 AngleXU=0 Radius=2.2
    g3: LineSegment StartX=-17.5 StartY=-40 StartZ=0 EndX=-17.5 EndY=-35 EndZ=0
    g4: ArcOfCircle CenterX=-17.5 CenterY=-33.5 CenterZ=0 NormalX=0 NormalY=0 NormalZ=1 AngleXU=0 Radius=5.5 StartAngle=0 EndAngle=3.14159
    g5: LineSegment StartX=-23 StartY=-33.5 StartZ=0 EndX=-12 EndY=-33.5 EndZ=0
    g6: LineSegment StartX=-23 StartY=-40 StartZ=0 EndX=-12 EndY=-40 EndZ=0
  constraints (20):
    c: PointOnObject(g0,g-3)
    c: Vertical(g0)
    c: PointOnObject(g1,g-3)
    c: Vertical(g1)
    c: Equal(g0,g1)
    c: Radius(g2) = 2.2
    c: PointOnObject(g3,g-3)
    c: Coincident(g3,g2)
    c: Symmetric(g0,g1,g3)
    c: DistanceX(g2,g-1) = 17.5
    c: DistanceY(g2,g-1) = 35
    c: Coincident(g4,g0)
    c: Coincident(g4,g1)
    c: Coincident(g5,g0)
    c: Coincident(g5,g1)
    c: PointOnObject(g4,g5)
    c: DistanceX(g5,g5) = 11
    c: DistanceY(g0,g0) = 6.5
    c: Coincident(g6,g0)
    c: Coincident(g6,g1)
FEATURE [PartDesign::Pad] Pad037
  BaseFeature = -> Mirrored003
  Direction = (1,1,1)
  Length = 4
  Length2 = 100
  Profile = -> Sketch098
  Reversed = true
  Type = 0
FEATURE [Sketcher::SketchObject] Sketch099
  ExternalGeometry = -> [Pad037]
  FullyConstrained = true
  MapMode = 5
  Placement = pos=(0,0,4) rot=(0,0,1;0rad)
  Support = -> [Pad037]
  sketch-geometry (7):
    g0: LineSegment StartX=-14 StartY=37.0207 StartZ=0 EndX=-17.5 EndY=39.0415 EndZ=0
    g1: LineSegment StartX=-17.5 StartY=39.0415 StartZ=0 EndX=-21 EndY=37.0207 EndZ=0
    g2: LineSegment StartX=-21 StartY=37.0207 StartZ=0 EndX=-21 EndY=32.9793 EndZ=0
    g3: LineSegment StartX=-21 StartY=32.9793 StartZ=0 EndX=-17.5 EndY=30.9585 EndZ=0
    g4: LineSegment StartX=-17.5 StartY=30.9585 StartZ=0 EndX=-14 EndY=32.9793 EndZ=0
    g5: LineSegment StartX=-14 StartY=32.9793 StartZ=0 EndX=-14 EndY=37.0207 EndZ=0
    g6: Circle CenterX=-17.5 CenterY=35 CenterZ=0 NormalX=0 NormalY=0 NormalZ=1 AngleXU=0 Radius=4.04145
  constraints (16):
    c: Coincident(g0,g1)
    c: Coincident(g1,g2)
    c: Coincident(g2,g3)
    c: Coincident(g3,g4)
    c: Coincident(g4,g5)
    c: Coincident(g5,g0)
    c: Equal(g0, g1-g5) x5
    c: PointOnObject(g0,g6)
    c: PointOnObject(g1,g6)
    c: PointOnObject(g2,g6)
    c: PointOnObject(g3,g6)
    c: PointOnObject(g4,g6)
    c: PointOnObject(g5,g6)
    c: Coincident(g6,g-3)
    c: Vertical(g5)
    c: DistanceX(g1,g0) = 7
FEATURE [PartDesign::Pocket] Pocket061
  BaseFeature = -> Pad037
  Length = 2.5
  Length2 = 100
  Profile = -> Sketch099
  Type = 0
FEATURE [PartDesign::Mirrored] Mirrored006
  BaseFeature = -> Pocket061
  MirrorPlane = -> Sketch098 [V_Axis]
  Originals = -> [Pad037,Pocket061]
FEATURE [PartDesign::Body] Body011  label="bottom_frame"
  Group = -> [Sketch081,Pad032,Sketch083,Pocket051,PolarPattern002,Sketch082,Pocket050,PolarPattern003,Sketch084,Pocket049,Mirrored003,Sketch098,Pad037,Sketch099,Pocket061,Mirrored006]
  Origin = -> Origin011
  Placement = pos=(0,0,-10) rot=(0,0,1;0rad)
  Tip = -> Mirrored006
